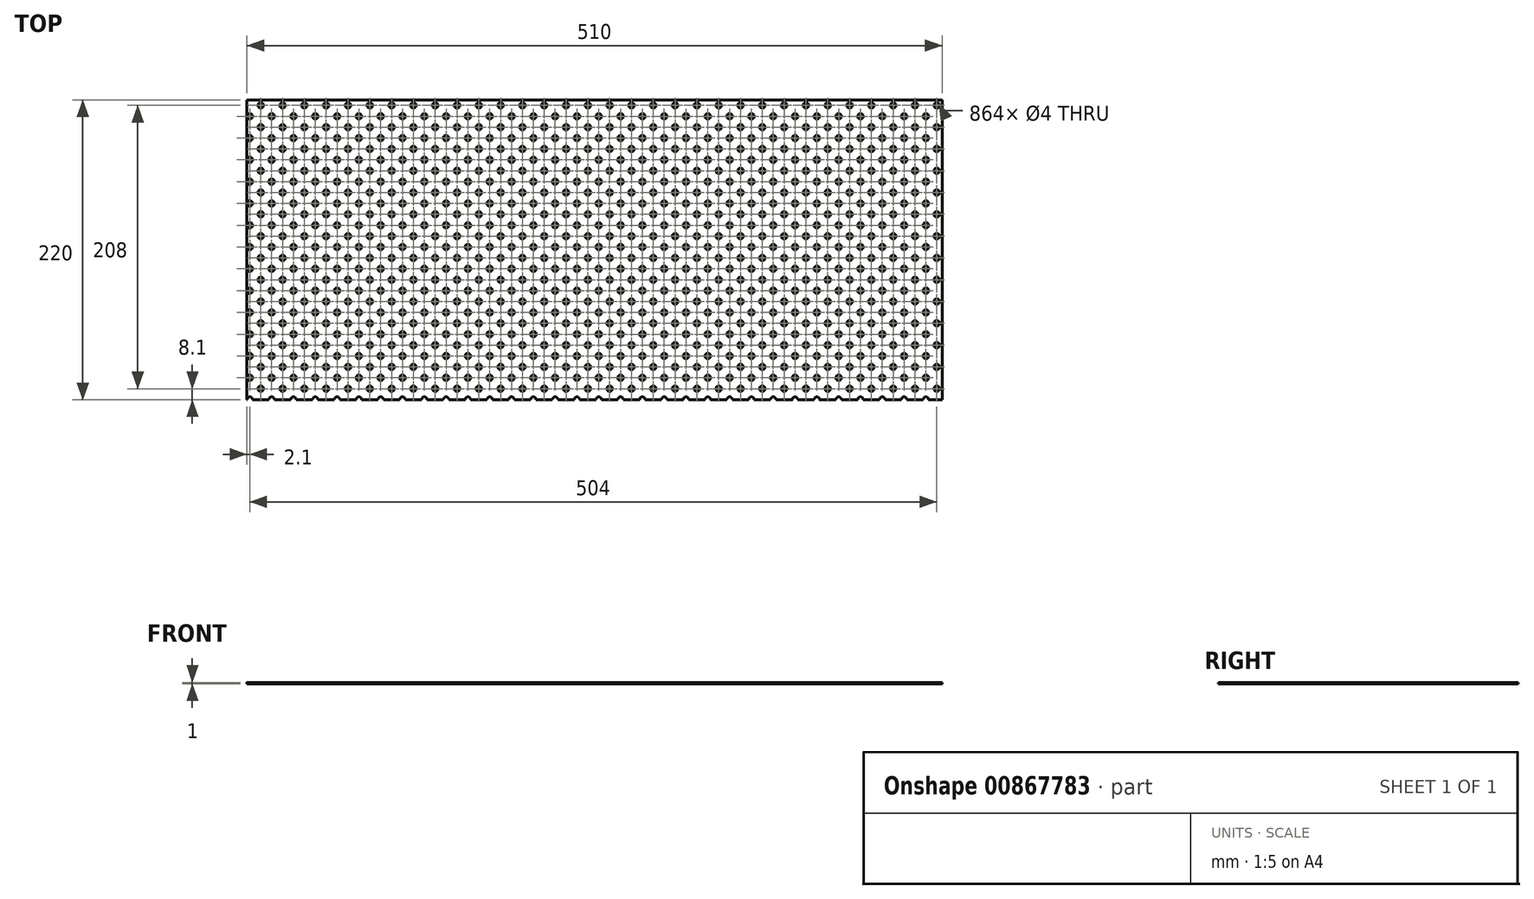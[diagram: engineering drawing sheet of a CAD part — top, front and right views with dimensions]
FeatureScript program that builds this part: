
annotation { "Feature Type Name" : "Feature", "Feature Type Description" : "" }
export const myFeature = defineFeature(function(context is Context, id is Id, definition is map)
    precondition{}
    {
        {
            var Q0;
            Q0=qCreatedBy(makeId("Top.planeOp"),FACE);
            var sketch = newSketch(context, id + "F0", { "sketchPlane" : qUnion([Q0])});
            skLineSegment(sketch, "E0.bottom", {"start": v(255, -110) * mm, "end": v(-255, -110) * mm});
            skLineSegment(sketch, "E0.top", {"start": v(255, 110) * mm, "end": v(-255, 110) * mm});
            skLineSegment(sketch, "E0.left", {"start": v(255, -110) * mm, "end": v(255, 110) * mm});
            skLineSegment(sketch, "E0.right", {"start": v(-255, -110) * mm, "end": v(-255, 110) * mm});
            skPoint(sketch, "E0.middle", {"position": v(0, 0) * mm});
            skCircle(sketch, "E1", {"center": v(-252.9, -109.9) * mm, "radius": 2 * mm});
            skCircle(sketch, "E2.0.1.0", {"center": v(-252.9, -93.9) * mm, "radius": 2 * mm});
            skCircle(sketch, "E2.0.2.0", {"center": v(-252.9, -77.9) * mm, "radius": 2 * mm});
            skCircle(sketch, "E2.0.3.0", {"center": v(-252.9, -61.9) * mm, "radius": 2 * mm});
            skCircle(sketch, "E2.0.4.0", {"center": v(-252.9, -45.9) * mm, "radius": 2 * mm});
            skCircle(sketch, "E2.0.5.0", {"center": v(-252.9, -29.9) * mm, "radius": 2 * mm});
            skCircle(sketch, "E2.0.6.0", {"center": v(-252.9, -13.9) * mm, "radius": 2 * mm});
            skCircle(sketch, "E2.0.7.0", {"center": v(-252.9, 2.1) * mm, "radius": 2 * mm});
            skCircle(sketch, "E2.1.0.0", {"center": v(-236.9, -109.9) * mm, "radius": 2 * mm});
            skCircle(sketch, "E2.1.1.0", {"center": v(-236.9, -93.9) * mm, "radius": 2 * mm});
            skCircle(sketch, "E2.1.2.0", {"center": v(-236.9, -77.9) * mm, "radius": 2 * mm});
            skCircle(sketch, "E2.1.3.0", {"center": v(-236.9, -61.9) * mm, "radius": 2 * mm});
            skCircle(sketch, "E2.1.4.0", {"center": v(-236.9, -45.9) * mm, "radius": 2 * mm});
            skCircle(sketch, "E2.1.5.0", {"center": v(-236.9, -29.9) * mm, "radius": 2 * mm});
            skCircle(sketch, "E2.1.6.0", {"center": v(-236.9, -13.9) * mm, "radius": 2 * mm});
            skCircle(sketch, "E2.1.7.0", {"center": v(-236.9, 2.1) * mm, "radius": 2 * mm});
            skCircle(sketch, "E2.2.0.0", {"center": v(-220.9, -109.9) * mm, "radius": 2 * mm});
            skCircle(sketch, "E2.2.1.0", {"center": v(-220.9, -93.9) * mm, "radius": 2 * mm});
            skCircle(sketch, "E2.2.2.0", {"center": v(-220.9, -77.9) * mm, "radius": 2 * mm});
            skCircle(sketch, "E2.2.3.0", {"center": v(-220.9, -61.9) * mm, "radius": 2 * mm});
            skCircle(sketch, "E2.2.4.0", {"center": v(-220.9, -45.9) * mm, "radius": 2 * mm});
            skCircle(sketch, "E2.2.5.0", {"center": v(-220.9, -29.9) * mm, "radius": 2 * mm});
            skCircle(sketch, "E2.2.6.0", {"center": v(-220.9, -13.9) * mm, "radius": 2 * mm});
            skCircle(sketch, "E2.2.7.0", {"center": v(-220.9, 2.1) * mm, "radius": 2 * mm});
            skCircle(sketch, "E2.3.0.0", {"center": v(-204.9, -109.9) * mm, "radius": 2 * mm});
            skCircle(sketch, "E2.3.1.0", {"center": v(-204.9, -93.9) * mm, "radius": 2 * mm});
            skCircle(sketch, "E2.3.2.0", {"center": v(-204.9, -77.9) * mm, "radius": 2 * mm});
            skCircle(sketch, "E2.3.3.0", {"center": v(-204.9, -61.9) * mm, "radius": 2 * mm});
            skCircle(sketch, "E2.3.4.0", {"center": v(-204.9, -45.9) * mm, "radius": 2 * mm});
            skCircle(sketch, "E2.3.5.0", {"center": v(-204.9, -29.9) * mm, "radius": 2 * mm});
            skCircle(sketch, "E2.3.6.0", {"center": v(-204.9, -13.9) * mm, "radius": 2 * mm});
            skCircle(sketch, "E2.3.7.0", {"center": v(-204.9, 2.1) * mm, "radius": 2 * mm});
            skCircle(sketch, "E2.4.0.0", {"center": v(-188.9, -109.9) * mm, "radius": 2 * mm});
            skCircle(sketch, "E2.4.1.0", {"center": v(-188.9, -93.9) * mm, "radius": 2 * mm});
            skCircle(sketch, "E2.4.2.0", {"center": v(-188.9, -77.9) * mm, "radius": 2 * mm});
            skCircle(sketch, "E2.4.3.0", {"center": v(-188.9, -61.9) * mm, "radius": 2 * mm});
            skCircle(sketch, "E2.4.4.0", {"center": v(-188.9, -45.9) * mm, "radius": 2 * mm});
            skCircle(sketch, "E2.4.5.0", {"center": v(-188.9, -29.9) * mm, "radius": 2 * mm});
            skCircle(sketch, "E2.4.6.0", {"center": v(-188.9, -13.9) * mm, "radius": 2 * mm});
            skCircle(sketch, "E2.4.7.0", {"center": v(-188.9, 2.1) * mm, "radius": 2 * mm});
            skCircle(sketch, "E2.5.0.0", {"center": v(-172.9, -109.9) * mm, "radius": 2 * mm});
            skCircle(sketch, "E2.5.1.0", {"center": v(-172.9, -93.9) * mm, "radius": 2 * mm});
            skCircle(sketch, "E2.5.2.0", {"center": v(-172.9, -77.9) * mm, "radius": 2 * mm});
            skCircle(sketch, "E2.5.3.0", {"center": v(-172.9, -61.9) * mm, "radius": 2 * mm});
            skCircle(sketch, "E2.5.4.0", {"center": v(-172.9, -45.9) * mm, "radius": 2 * mm});
            skCircle(sketch, "E2.5.5.0", {"center": v(-172.9, -29.9) * mm, "radius": 2 * mm});
            skCircle(sketch, "E2.5.6.0", {"center": v(-172.9, -13.9) * mm, "radius": 2 * mm});
            skCircle(sketch, "E2.5.7.0", {"center": v(-172.9, 2.1) * mm, "radius": 2 * mm});
            skCircle(sketch, "E2.6.0.0", {"center": v(-156.9, -109.9) * mm, "radius": 2 * mm});
            skCircle(sketch, "E2.6.1.0", {"center": v(-156.9, -93.9) * mm, "radius": 2 * mm});
            skCircle(sketch, "E2.6.2.0", {"center": v(-156.9, -77.9) * mm, "radius": 2 * mm});
            skCircle(sketch, "E2.6.3.0", {"center": v(-156.9, -61.9) * mm, "radius": 2 * mm});
            skCircle(sketch, "E2.6.4.0", {"center": v(-156.9, -45.9) * mm, "radius": 2 * mm});
            skCircle(sketch, "E2.6.5.0", {"center": v(-156.9, -29.9) * mm, "radius": 2 * mm});
            skCircle(sketch, "E2.6.6.0", {"center": v(-156.9, -13.9) * mm, "radius": 2 * mm});
            skCircle(sketch, "E2.6.7.0", {"center": v(-156.9, 2.1) * mm, "radius": 2 * mm});
            skCircle(sketch, "E2.7.0.0", {"center": v(-140.9, -109.9) * mm, "radius": 2 * mm});
            skCircle(sketch, "E2.7.1.0", {"center": v(-140.9, -93.9) * mm, "radius": 2 * mm});
            skCircle(sketch, "E2.7.2.0", {"center": v(-140.9, -77.9) * mm, "radius": 2 * mm});
            skCircle(sketch, "E2.7.3.0", {"center": v(-140.9, -61.9) * mm, "radius": 2 * mm});
            skCircle(sketch, "E2.7.4.0", {"center": v(-140.9, -45.9) * mm, "radius": 2 * mm});
            skCircle(sketch, "E2.7.5.0", {"center": v(-140.9, -29.9) * mm, "radius": 2 * mm});
            skCircle(sketch, "E2.7.6.0", {"center": v(-140.9, -13.9) * mm, "radius": 2 * mm});
            skCircle(sketch, "E2.7.7.0", {"center": v(-140.9, 2.1) * mm, "radius": 2 * mm});
            skCircle(sketch, "E2.8.0.0", {"center": v(-124.9, -109.9) * mm, "radius": 2 * mm});
            skCircle(sketch, "E2.8.1.0", {"center": v(-124.9, -93.9) * mm, "radius": 2 * mm});
            skCircle(sketch, "E2.8.2.0", {"center": v(-124.9, -77.9) * mm, "radius": 2 * mm});
            skCircle(sketch, "E2.8.3.0", {"center": v(-124.9, -61.9) * mm, "radius": 2 * mm});
            skCircle(sketch, "E2.8.4.0", {"center": v(-124.9, -45.9) * mm, "radius": 2 * mm});
            skCircle(sketch, "E2.8.5.0", {"center": v(-124.9, -29.9) * mm, "radius": 2 * mm});
            skCircle(sketch, "E2.8.6.0", {"center": v(-124.9, -13.9) * mm, "radius": 2 * mm});
            skCircle(sketch, "E2.8.7.0", {"center": v(-124.9, 2.1) * mm, "radius": 2 * mm});
            skCircle(sketch, "E2.9.0.0", {"center": v(-108.9, -109.9) * mm, "radius": 2 * mm});
            skCircle(sketch, "E2.9.1.0", {"center": v(-108.9, -93.9) * mm, "radius": 2 * mm});
            skCircle(sketch, "E2.9.2.0", {"center": v(-108.9, -77.9) * mm, "radius": 2 * mm});
            skCircle(sketch, "E2.9.3.0", {"center": v(-108.9, -61.9) * mm, "radius": 2 * mm});
            skCircle(sketch, "E2.9.4.0", {"center": v(-108.9, -45.9) * mm, "radius": 2 * mm});
            skCircle(sketch, "E2.9.5.0", {"center": v(-108.9, -29.9) * mm, "radius": 2 * mm});
            skCircle(sketch, "E2.9.6.0", {"center": v(-108.9, -13.9) * mm, "radius": 2 * mm});
            skCircle(sketch, "E2.9.7.0", {"center": v(-108.9, 2.1) * mm, "radius": 2 * mm});
            skCircle(sketch, "E2.10.0.0", {"center": v(-92.9, -109.9) * mm, "radius": 2 * mm});
            skCircle(sketch, "E2.10.1.0", {"center": v(-92.9, -93.9) * mm, "radius": 2 * mm});
            skCircle(sketch, "E2.10.2.0", {"center": v(-92.9, -77.9) * mm, "radius": 2 * mm});
            skCircle(sketch, "E2.10.3.0", {"center": v(-92.9, -61.9) * mm, "radius": 2 * mm});
            skCircle(sketch, "E2.10.4.0", {"center": v(-92.9, -45.9) * mm, "radius": 2 * mm});
            skCircle(sketch, "E2.10.5.0", {"center": v(-92.9, -29.9) * mm, "radius": 2 * mm});
            skCircle(sketch, "E2.10.6.0", {"center": v(-92.9, -13.9) * mm, "radius": 2 * mm});
            skCircle(sketch, "E2.10.7.0", {"center": v(-92.9, 2.1) * mm, "radius": 2 * mm});
            skCircle(sketch, "E2.11.0.0", {"center": v(-76.9, -109.9) * mm, "radius": 2 * mm});
            skCircle(sketch, "E2.11.1.0", {"center": v(-76.9, -93.9) * mm, "radius": 2 * mm});
            skCircle(sketch, "E2.11.2.0", {"center": v(-76.9, -77.9) * mm, "radius": 2 * mm});
            skCircle(sketch, "E2.11.3.0", {"center": v(-76.9, -61.9) * mm, "radius": 2 * mm});
            skCircle(sketch, "E2.11.4.0", {"center": v(-76.9, -45.9) * mm, "radius": 2 * mm});
            skCircle(sketch, "E2.11.5.0", {"center": v(-76.9, -29.9) * mm, "radius": 2 * mm});
            skCircle(sketch, "E2.11.6.0", {"center": v(-76.9, -13.9) * mm, "radius": 2 * mm});
            skCircle(sketch, "E2.11.7.0", {"center": v(-76.9, 2.1) * mm, "radius": 2 * mm});
            skCircle(sketch, "E2.12.0.0", {"center": v(-60.9, -109.9) * mm, "radius": 2 * mm});
            skCircle(sketch, "E2.12.1.0", {"center": v(-60.9, -93.9) * mm, "radius": 2 * mm});
            skCircle(sketch, "E2.12.2.0", {"center": v(-60.9, -77.9) * mm, "radius": 2 * mm});
            skCircle(sketch, "E2.12.3.0", {"center": v(-60.9, -61.9) * mm, "radius": 2 * mm});
            skCircle(sketch, "E2.12.4.0", {"center": v(-60.9, -45.9) * mm, "radius": 2 * mm});
            skCircle(sketch, "E2.12.5.0", {"center": v(-60.9, -29.9) * mm, "radius": 2 * mm});
            skCircle(sketch, "E2.12.6.0", {"center": v(-60.9, -13.9) * mm, "radius": 2 * mm});
            skCircle(sketch, "E2.12.7.0", {"center": v(-60.9, 2.1) * mm, "radius": 2 * mm});
            skCircle(sketch, "E2.13.0.0", {"center": v(-44.9, -109.9) * mm, "radius": 2 * mm});
            skCircle(sketch, "E2.13.1.0", {"center": v(-44.9, -93.9) * mm, "radius": 2 * mm});
            skCircle(sketch, "E2.13.2.0", {"center": v(-44.9, -77.9) * mm, "radius": 2 * mm});
            skCircle(sketch, "E2.13.3.0", {"center": v(-44.9, -61.9) * mm, "radius": 2 * mm});
            skCircle(sketch, "E2.13.4.0", {"center": v(-44.9, -45.9) * mm, "radius": 2 * mm});
            skCircle(sketch, "E2.13.5.0", {"center": v(-44.9, -29.9) * mm, "radius": 2 * mm});
            skCircle(sketch, "E2.13.6.0", {"center": v(-44.9, -13.9) * mm, "radius": 2 * mm});
            skCircle(sketch, "E2.13.7.0", {"center": v(-44.9, 2.1) * mm, "radius": 2 * mm});
            skCircle(sketch, "E2.14.0.0", {"center": v(-28.9, -109.9) * mm, "radius": 2 * mm});
            skCircle(sketch, "E2.14.1.0", {"center": v(-28.9, -93.9) * mm, "radius": 2 * mm});
            skCircle(sketch, "E2.14.2.0", {"center": v(-28.9, -77.9) * mm, "radius": 2 * mm});
            skCircle(sketch, "E2.14.3.0", {"center": v(-28.9, -61.9) * mm, "radius": 2 * mm});
            skCircle(sketch, "E2.14.4.0", {"center": v(-28.9, -45.9) * mm, "radius": 2 * mm});
            skCircle(sketch, "E2.14.5.0", {"center": v(-28.9, -29.9) * mm, "radius": 2 * mm});
            skCircle(sketch, "E2.14.6.0", {"center": v(-28.9, -13.9) * mm, "radius": 2 * mm});
            skCircle(sketch, "E2.14.7.0", {"center": v(-28.9, 2.1) * mm, "radius": 2 * mm});
            skCircle(sketch, "E2.15.0.0", {"center": v(-12.9, -109.9) * mm, "radius": 2 * mm});
            skCircle(sketch, "E2.15.1.0", {"center": v(-12.9, -93.9) * mm, "radius": 2 * mm});
            skCircle(sketch, "E2.15.2.0", {"center": v(-12.9, -77.9) * mm, "radius": 2 * mm});
            skCircle(sketch, "E2.15.3.0", {"center": v(-12.9, -61.9) * mm, "radius": 2 * mm});
            skCircle(sketch, "E2.15.4.0", {"center": v(-12.9, -45.9) * mm, "radius": 2 * mm});
            skCircle(sketch, "E2.15.5.0", {"center": v(-12.9, -29.9) * mm, "radius": 2 * mm});
            skCircle(sketch, "E2.15.6.0", {"center": v(-12.9, -13.9) * mm, "radius": 2 * mm});
            skCircle(sketch, "E2.15.7.0", {"center": v(-12.9, 2.1) * mm, "radius": 2 * mm});
            skCircle(sketch, "E2.16.0.0", {"center": v(3.1, -109.9) * mm, "radius": 2 * mm});
            skCircle(sketch, "E2.16.1.0", {"center": v(3.1, -93.9) * mm, "radius": 2 * mm});
            skCircle(sketch, "E2.16.2.0", {"center": v(3.1, -77.9) * mm, "radius": 2 * mm});
            skCircle(sketch, "E2.16.3.0", {"center": v(3.1, -61.9) * mm, "radius": 2 * mm});
            skCircle(sketch, "E2.16.4.0", {"center": v(3.1, -45.9) * mm, "radius": 2 * mm});
            skCircle(sketch, "E2.16.5.0", {"center": v(3.1, -29.9) * mm, "radius": 2 * mm});
            skCircle(sketch, "E2.16.6.0", {"center": v(3.1, -13.9) * mm, "radius": 2 * mm});
            skCircle(sketch, "E2.16.7.0", {"center": v(3.1, 2.1) * mm, "radius": 2 * mm});
            skCircle(sketch, "E2.17.0.0", {"center": v(19.1, -109.9) * mm, "radius": 2 * mm});
            skCircle(sketch, "E2.17.1.0", {"center": v(19.1, -93.9) * mm, "radius": 2 * mm});
            skCircle(sketch, "E2.17.2.0", {"center": v(19.1, -77.9) * mm, "radius": 2 * mm});
            skCircle(sketch, "E2.17.3.0", {"center": v(19.1, -61.9) * mm, "radius": 2 * mm});
            skCircle(sketch, "E2.17.4.0", {"center": v(19.1, -45.9) * mm, "radius": 2 * mm});
            skCircle(sketch, "E2.17.5.0", {"center": v(19.1, -29.9) * mm, "radius": 2 * mm});
            skCircle(sketch, "E2.17.6.0", {"center": v(19.1, -13.9) * mm, "radius": 2 * mm});
            skCircle(sketch, "E2.17.7.0", {"center": v(19.1, 2.1) * mm, "radius": 2 * mm});
            skCircle(sketch, "E2.18.0.0", {"center": v(35.1, -109.9) * mm, "radius": 2 * mm});
            skCircle(sketch, "E2.18.1.0", {"center": v(35.1, -93.9) * mm, "radius": 2 * mm});
            skCircle(sketch, "E2.18.2.0", {"center": v(35.1, -77.9) * mm, "radius": 2 * mm});
            skCircle(sketch, "E2.18.3.0", {"center": v(35.1, -61.9) * mm, "radius": 2 * mm});
            skCircle(sketch, "E2.18.4.0", {"center": v(35.1, -45.9) * mm, "radius": 2 * mm});
            skCircle(sketch, "E2.18.5.0", {"center": v(35.1, -29.9) * mm, "radius": 2 * mm});
            skCircle(sketch, "E2.18.6.0", {"center": v(35.1, -13.9) * mm, "radius": 2 * mm});
            skCircle(sketch, "E2.18.7.0", {"center": v(35.1, 2.1) * mm, "radius": 2 * mm});
            skCircle(sketch, "E2.19.0.0", {"center": v(51.1, -109.9) * mm, "radius": 2 * mm});
            skCircle(sketch, "E2.19.1.0", {"center": v(51.1, -93.9) * mm, "radius": 2 * mm});
            skCircle(sketch, "E2.19.2.0", {"center": v(51.1, -77.9) * mm, "radius": 2 * mm});
            skCircle(sketch, "E2.19.3.0", {"center": v(51.1, -61.9) * mm, "radius": 2 * mm});
            skCircle(sketch, "E2.19.4.0", {"center": v(51.1, -45.9) * mm, "radius": 2 * mm});
            skCircle(sketch, "E2.19.5.0", {"center": v(51.1, -29.9) * mm, "radius": 2 * mm});
            skCircle(sketch, "E2.19.6.0", {"center": v(51.1, -13.9) * mm, "radius": 2 * mm});
            skCircle(sketch, "E2.19.7.0", {"center": v(51.1, 2.1) * mm, "radius": 2 * mm});
            skCircle(sketch, "E2.20.0.0", {"center": v(67.1, -109.9) * mm, "radius": 2 * mm});
            skCircle(sketch, "E2.20.1.0", {"center": v(67.1, -93.9) * mm, "radius": 2 * mm});
            skCircle(sketch, "E2.20.2.0", {"center": v(67.1, -77.9) * mm, "radius": 2 * mm});
            skCircle(sketch, "E2.20.3.0", {"center": v(67.1, -61.9) * mm, "radius": 2 * mm});
            skCircle(sketch, "E2.20.4.0", {"center": v(67.1, -45.9) * mm, "radius": 2 * mm});
            skCircle(sketch, "E2.20.5.0", {"center": v(67.1, -29.9) * mm, "radius": 2 * mm});
            skCircle(sketch, "E2.20.6.0", {"center": v(67.1, -13.9) * mm, "radius": 2 * mm});
            skCircle(sketch, "E2.20.7.0", {"center": v(67.1, 2.1) * mm, "radius": 2 * mm});
            skCircle(sketch, "E2.21.0.0", {"center": v(83.1, -109.9) * mm, "radius": 2 * mm});
            skCircle(sketch, "E2.21.1.0", {"center": v(83.1, -93.9) * mm, "radius": 2 * mm});
            skCircle(sketch, "E2.21.2.0", {"center": v(83.1, -77.9) * mm, "radius": 2 * mm});
            skCircle(sketch, "E2.21.3.0", {"center": v(83.1, -61.9) * mm, "radius": 2 * mm});
            skCircle(sketch, "E2.21.4.0", {"center": v(83.1, -45.9) * mm, "radius": 2 * mm});
            skCircle(sketch, "E2.21.5.0", {"center": v(83.1, -29.9) * mm, "radius": 2 * mm});
            skCircle(sketch, "E2.21.6.0", {"center": v(83.1, -13.9) * mm, "radius": 2 * mm});
            skCircle(sketch, "E2.21.7.0", {"center": v(83.1, 2.1) * mm, "radius": 2 * mm});
            skCircle(sketch, "E2.22.0.0", {"center": v(99.1, -109.9) * mm, "radius": 2 * mm});
            skCircle(sketch, "E2.22.1.0", {"center": v(99.1, -93.9) * mm, "radius": 2 * mm});
            skCircle(sketch, "E2.22.2.0", {"center": v(99.1, -77.9) * mm, "radius": 2 * mm});
            skCircle(sketch, "E2.22.3.0", {"center": v(99.1, -61.9) * mm, "radius": 2 * mm});
            skCircle(sketch, "E2.22.4.0", {"center": v(99.1, -45.9) * mm, "radius": 2 * mm});
            skCircle(sketch, "E2.22.5.0", {"center": v(99.1, -29.9) * mm, "radius": 2 * mm});
            skCircle(sketch, "E2.22.6.0", {"center": v(99.1, -13.9) * mm, "radius": 2 * mm});
            skCircle(sketch, "E2.22.7.0", {"center": v(99.1, 2.1) * mm, "radius": 2 * mm});
            skCircle(sketch, "E2.23.0.0", {"center": v(115.1, -109.9) * mm, "radius": 2 * mm});
            skCircle(sketch, "E2.23.1.0", {"center": v(115.1, -93.9) * mm, "radius": 2 * mm});
            skCircle(sketch, "E2.23.2.0", {"center": v(115.1, -77.9) * mm, "radius": 2 * mm});
            skCircle(sketch, "E2.23.3.0", {"center": v(115.1, -61.9) * mm, "radius": 2 * mm});
            skCircle(sketch, "E2.23.4.0", {"center": v(115.1, -45.9) * mm, "radius": 2 * mm});
            skCircle(sketch, "E2.23.5.0", {"center": v(115.1, -29.9) * mm, "radius": 2 * mm});
            skCircle(sketch, "E2.23.6.0", {"center": v(115.1, -13.9) * mm, "radius": 2 * mm});
            skCircle(sketch, "E2.23.7.0", {"center": v(115.1, 2.1) * mm, "radius": 2 * mm});
            skCircle(sketch, "E2.24.0.0", {"center": v(131.1, -109.9) * mm, "radius": 2 * mm});
            skCircle(sketch, "E2.24.1.0", {"center": v(131.1, -93.9) * mm, "radius": 2 * mm});
            skCircle(sketch, "E2.24.2.0", {"center": v(131.1, -77.9) * mm, "radius": 2 * mm});
            skCircle(sketch, "E2.24.3.0", {"center": v(131.1, -61.9) * mm, "radius": 2 * mm});
            skCircle(sketch, "E2.24.4.0", {"center": v(131.1, -45.9) * mm, "radius": 2 * mm});
            skCircle(sketch, "E2.24.5.0", {"center": v(131.1, -29.9) * mm, "radius": 2 * mm});
            skCircle(sketch, "E2.24.6.0", {"center": v(131.1, -13.9) * mm, "radius": 2 * mm});
            skCircle(sketch, "E2.24.7.0", {"center": v(131.1, 2.1) * mm, "radius": 2 * mm});
            skCircle(sketch, "E2.25.0.0", {"center": v(147.1, -109.9) * mm, "radius": 2 * mm});
            skCircle(sketch, "E2.25.1.0", {"center": v(147.1, -93.9) * mm, "radius": 2 * mm});
            skCircle(sketch, "E2.25.2.0", {"center": v(147.1, -77.9) * mm, "radius": 2 * mm});
            skCircle(sketch, "E2.25.3.0", {"center": v(147.1, -61.9) * mm, "radius": 2 * mm});
            skCircle(sketch, "E2.25.4.0", {"center": v(147.1, -45.9) * mm, "radius": 2 * mm});
            skCircle(sketch, "E2.25.5.0", {"center": v(147.1, -29.9) * mm, "radius": 2 * mm});
            skCircle(sketch, "E2.25.6.0", {"center": v(147.1, -13.9) * mm, "radius": 2 * mm});
            skCircle(sketch, "E2.25.7.0", {"center": v(147.1, 2.1) * mm, "radius": 2 * mm});
            skCircle(sketch, "E2.26.0.0", {"center": v(163.1, -109.9) * mm, "radius": 2 * mm});
            skCircle(sketch, "E2.26.1.0", {"center": v(163.1, -93.9) * mm, "radius": 2 * mm});
            skCircle(sketch, "E2.26.2.0", {"center": v(163.1, -77.9) * mm, "radius": 2 * mm});
            skCircle(sketch, "E2.26.3.0", {"center": v(163.1, -61.9) * mm, "radius": 2 * mm});
            skCircle(sketch, "E2.26.4.0", {"center": v(163.1, -45.9) * mm, "radius": 2 * mm});
            skCircle(sketch, "E2.26.5.0", {"center": v(163.1, -29.9) * mm, "radius": 2 * mm});
            skCircle(sketch, "E2.26.6.0", {"center": v(163.1, -13.9) * mm, "radius": 2 * mm});
            skCircle(sketch, "E2.26.7.0", {"center": v(163.1, 2.1) * mm, "radius": 2 * mm});
            skCircle(sketch, "E2.27.0.0", {"center": v(179.1, -109.9) * mm, "radius": 2 * mm});
            skCircle(sketch, "E2.27.1.0", {"center": v(179.1, -93.9) * mm, "radius": 2 * mm});
            skCircle(sketch, "E2.27.2.0", {"center": v(179.1, -77.9) * mm, "radius": 2 * mm});
            skCircle(sketch, "E2.27.3.0", {"center": v(179.1, -61.9) * mm, "radius": 2 * mm});
            skCircle(sketch, "E2.27.4.0", {"center": v(179.1, -45.9) * mm, "radius": 2 * mm});
            skCircle(sketch, "E2.27.5.0", {"center": v(179.1, -29.9) * mm, "radius": 2 * mm});
            skCircle(sketch, "E2.27.6.0", {"center": v(179.1, -13.9) * mm, "radius": 2 * mm});
            skCircle(sketch, "E2.27.7.0", {"center": v(179.1, 2.1) * mm, "radius": 2 * mm});
            skCircle(sketch, "E2.28.0.0", {"center": v(195.1, -109.9) * mm, "radius": 2 * mm});
            skCircle(sketch, "E2.28.1.0", {"center": v(195.1, -93.9) * mm, "radius": 2 * mm});
            skCircle(sketch, "E2.28.2.0", {"center": v(195.1, -77.9) * mm, "radius": 2 * mm});
            skCircle(sketch, "E2.28.3.0", {"center": v(195.1, -61.9) * mm, "radius": 2 * mm});
            skCircle(sketch, "E2.28.4.0", {"center": v(195.1, -45.9) * mm, "radius": 2 * mm});
            skCircle(sketch, "E2.28.5.0", {"center": v(195.1, -29.9) * mm, "radius": 2 * mm});
            skCircle(sketch, "E2.28.6.0", {"center": v(195.1, -13.9) * mm, "radius": 2 * mm});
            skCircle(sketch, "E2.28.7.0", {"center": v(195.1, 2.1) * mm, "radius": 2 * mm});
            skCircle(sketch, "E2.29.0.0", {"center": v(211.1, -109.9) * mm, "radius": 2 * mm});
            skCircle(sketch, "E2.29.1.0", {"center": v(211.1, -93.9) * mm, "radius": 2 * mm});
            skCircle(sketch, "E2.29.2.0", {"center": v(211.1, -77.9) * mm, "radius": 2 * mm});
            skCircle(sketch, "E2.29.3.0", {"center": v(211.1, -61.9) * mm, "radius": 2 * mm});
            skCircle(sketch, "E2.29.4.0", {"center": v(211.1, -45.9) * mm, "radius": 2 * mm});
            skCircle(sketch, "E2.29.5.0", {"center": v(211.1, -29.9) * mm, "radius": 2 * mm});
            skCircle(sketch, "E2.29.6.0", {"center": v(211.1, -13.9) * mm, "radius": 2 * mm});
            skCircle(sketch, "E2.29.7.0", {"center": v(211.1, 2.1) * mm, "radius": 2 * mm});
            skCircle(sketch, "E2.30.0.0", {"center": v(227.1, -109.9) * mm, "radius": 2 * mm});
            skCircle(sketch, "E2.30.1.0", {"center": v(227.1, -93.9) * mm, "radius": 2 * mm});
            skCircle(sketch, "E2.30.2.0", {"center": v(227.1, -77.9) * mm, "radius": 2 * mm});
            skCircle(sketch, "E2.30.3.0", {"center": v(227.1, -61.9) * mm, "radius": 2 * mm});
            skCircle(sketch, "E2.30.4.0", {"center": v(227.1, -45.9) * mm, "radius": 2 * mm});
            skCircle(sketch, "E2.30.5.0", {"center": v(227.1, -29.9) * mm, "radius": 2 * mm});
            skCircle(sketch, "E2.30.6.0", {"center": v(227.1, -13.9) * mm, "radius": 2 * mm});
            skCircle(sketch, "E2.30.7.0", {"center": v(227.1, 2.1) * mm, "radius": 2 * mm});
            skLineSegment(sketch, "E2.direction1", {"start": v(-252.9, -109.9) * mm, "end": v(-236.9, -109.9) * mm, "construction": true});
            skLineSegment(sketch, "E2.direction2", {"start": v(-252.9, -109.9) * mm, "end": v(-252.9, -93.9) * mm, "construction": true});
            skCircle(sketch, "E3", {"center": v(-244.9, -101.9) * mm, "radius": 2 * mm});
            skCircle(sketch, "E4.0.1.0", {"center": v(-244.9, -85.9) * mm, "radius": 2 * mm});
            skCircle(sketch, "E4.0.2.0", {"center": v(-244.9, -69.9) * mm, "radius": 2 * mm});
            skCircle(sketch, "E4.0.3.0", {"center": v(-244.9, -53.9) * mm, "radius": 2 * mm});
            skCircle(sketch, "E4.0.4.0", {"center": v(-244.9, -37.9) * mm, "radius": 2 * mm});
            skCircle(sketch, "E4.0.5.0", {"center": v(-244.9, -21.9) * mm, "radius": 2 * mm});
            skCircle(sketch, "E4.1.0.0", {"center": v(-228.9, -101.9) * mm, "radius": 2 * mm});
            skCircle(sketch, "E4.1.1.0", {"center": v(-228.9, -85.9) * mm, "radius": 2 * mm});
            skCircle(sketch, "E4.1.2.0", {"center": v(-228.9, -69.9) * mm, "radius": 2 * mm});
            skCircle(sketch, "E4.1.3.0", {"center": v(-228.9, -53.9) * mm, "radius": 2 * mm});
            skCircle(sketch, "E4.1.4.0", {"center": v(-228.9, -37.9) * mm, "radius": 2 * mm});
            skCircle(sketch, "E4.1.5.0", {"center": v(-228.9, -21.9) * mm, "radius": 2 * mm});
            skCircle(sketch, "E4.2.0.0", {"center": v(-212.9, -101.9) * mm, "radius": 2 * mm});
            skCircle(sketch, "E4.2.1.0", {"center": v(-212.9, -85.9) * mm, "radius": 2 * mm});
            skCircle(sketch, "E4.2.2.0", {"center": v(-212.9, -69.9) * mm, "radius": 2 * mm});
            skCircle(sketch, "E4.2.3.0", {"center": v(-212.9, -53.9) * mm, "radius": 2 * mm});
            skCircle(sketch, "E4.2.4.0", {"center": v(-212.9, -37.9) * mm, "radius": 2 * mm});
            skCircle(sketch, "E4.2.5.0", {"center": v(-212.9, -21.9) * mm, "radius": 2 * mm});
            skCircle(sketch, "E4.3.0.0", {"center": v(-196.9, -101.9) * mm, "radius": 2 * mm});
            skCircle(sketch, "E4.3.1.0", {"center": v(-196.9, -85.9) * mm, "radius": 2 * mm});
            skCircle(sketch, "E4.3.2.0", {"center": v(-196.9, -69.9) * mm, "radius": 2 * mm});
            skCircle(sketch, "E4.3.3.0", {"center": v(-196.9, -53.9) * mm, "radius": 2 * mm});
            skCircle(sketch, "E4.3.4.0", {"center": v(-196.9, -37.9) * mm, "radius": 2 * mm});
            skCircle(sketch, "E4.3.5.0", {"center": v(-196.9, -21.9) * mm, "radius": 2 * mm});
            skCircle(sketch, "E4.4.0.0", {"center": v(-180.9, -101.9) * mm, "radius": 2 * mm});
            skCircle(sketch, "E4.4.1.0", {"center": v(-180.9, -85.9) * mm, "radius": 2 * mm});
            skCircle(sketch, "E4.4.2.0", {"center": v(-180.9, -69.9) * mm, "radius": 2 * mm});
            skCircle(sketch, "E4.4.3.0", {"center": v(-180.9, -53.9) * mm, "radius": 2 * mm});
            skCircle(sketch, "E4.4.4.0", {"center": v(-180.9, -37.9) * mm, "radius": 2 * mm});
            skCircle(sketch, "E4.4.5.0", {"center": v(-180.9, -21.9) * mm, "radius": 2 * mm});
            skCircle(sketch, "E4.5.0.0", {"center": v(-164.9, -101.9) * mm, "radius": 2 * mm});
            skCircle(sketch, "E4.5.1.0", {"center": v(-164.9, -85.9) * mm, "radius": 2 * mm});
            skCircle(sketch, "E4.5.2.0", {"center": v(-164.9, -69.9) * mm, "radius": 2 * mm});
            skCircle(sketch, "E4.5.3.0", {"center": v(-164.9, -53.9) * mm, "radius": 2 * mm});
            skCircle(sketch, "E4.5.4.0", {"center": v(-164.9, -37.9) * mm, "radius": 2 * mm});
            skCircle(sketch, "E4.5.5.0", {"center": v(-164.9, -21.9) * mm, "radius": 2 * mm});
            skCircle(sketch, "E4.6.0.0", {"center": v(-148.9, -101.9) * mm, "radius": 2 * mm});
            skCircle(sketch, "E4.6.1.0", {"center": v(-148.9, -85.9) * mm, "radius": 2 * mm});
            skCircle(sketch, "E4.6.2.0", {"center": v(-148.9, -69.9) * mm, "radius": 2 * mm});
            skCircle(sketch, "E4.6.3.0", {"center": v(-148.9, -53.9) * mm, "radius": 2 * mm});
            skCircle(sketch, "E4.6.4.0", {"center": v(-148.9, -37.9) * mm, "radius": 2 * mm});
            skCircle(sketch, "E4.6.5.0", {"center": v(-148.9, -21.9) * mm, "radius": 2 * mm});
            skCircle(sketch, "E4.7.0.0", {"center": v(-132.9, -101.9) * mm, "radius": 2 * mm});
            skCircle(sketch, "E4.7.1.0", {"center": v(-132.9, -85.9) * mm, "radius": 2 * mm});
            skCircle(sketch, "E4.7.2.0", {"center": v(-132.9, -69.9) * mm, "radius": 2 * mm});
            skCircle(sketch, "E4.7.3.0", {"center": v(-132.9, -53.9) * mm, "radius": 2 * mm});
            skCircle(sketch, "E4.7.4.0", {"center": v(-132.9, -37.9) * mm, "radius": 2 * mm});
            skCircle(sketch, "E4.7.5.0", {"center": v(-132.9, -21.9) * mm, "radius": 2 * mm});
            skCircle(sketch, "E4.8.0.0", {"center": v(-116.9, -101.9) * mm, "radius": 2 * mm});
            skCircle(sketch, "E4.8.1.0", {"center": v(-116.9, -85.9) * mm, "radius": 2 * mm});
            skCircle(sketch, "E4.8.2.0", {"center": v(-116.9, -69.9) * mm, "radius": 2 * mm});
            skCircle(sketch, "E4.8.3.0", {"center": v(-116.9, -53.9) * mm, "radius": 2 * mm});
            skCircle(sketch, "E4.8.4.0", {"center": v(-116.9, -37.9) * mm, "radius": 2 * mm});
            skCircle(sketch, "E4.8.5.0", {"center": v(-116.9, -21.9) * mm, "radius": 2 * mm});
            skCircle(sketch, "E4.9.0.0", {"center": v(-100.9, -101.9) * mm, "radius": 2 * mm});
            skCircle(sketch, "E4.9.1.0", {"center": v(-100.9, -85.9) * mm, "radius": 2 * mm});
            skCircle(sketch, "E4.9.2.0", {"center": v(-100.9, -69.9) * mm, "radius": 2 * mm});
            skCircle(sketch, "E4.9.3.0", {"center": v(-100.9, -53.9) * mm, "radius": 2 * mm});
            skCircle(sketch, "E4.9.4.0", {"center": v(-100.9, -37.9) * mm, "radius": 2 * mm});
            skCircle(sketch, "E4.9.5.0", {"center": v(-100.9, -21.9) * mm, "radius": 2 * mm});
            skCircle(sketch, "E4.10.0.0", {"center": v(-84.9, -101.9) * mm, "radius": 2 * mm});
            skCircle(sketch, "E4.10.1.0", {"center": v(-84.9, -85.9) * mm, "radius": 2 * mm});
            skCircle(sketch, "E4.10.2.0", {"center": v(-84.9, -69.9) * mm, "radius": 2 * mm});
            skCircle(sketch, "E4.10.3.0", {"center": v(-84.9, -53.9) * mm, "radius": 2 * mm});
            skCircle(sketch, "E4.10.4.0", {"center": v(-84.9, -37.9) * mm, "radius": 2 * mm});
            skCircle(sketch, "E4.10.5.0", {"center": v(-84.9, -21.9) * mm, "radius": 2 * mm});
            skCircle(sketch, "E4.11.0.0", {"center": v(-68.9, -101.9) * mm, "radius": 2 * mm});
            skCircle(sketch, "E4.11.1.0", {"center": v(-68.9, -85.9) * mm, "radius": 2 * mm});
            skCircle(sketch, "E4.11.2.0", {"center": v(-68.9, -69.9) * mm, "radius": 2 * mm});
            skCircle(sketch, "E4.11.3.0", {"center": v(-68.9, -53.9) * mm, "radius": 2 * mm});
            skCircle(sketch, "E4.11.4.0", {"center": v(-68.9, -37.9) * mm, "radius": 2 * mm});
            skCircle(sketch, "E4.11.5.0", {"center": v(-68.9, -21.9) * mm, "radius": 2 * mm});
            skCircle(sketch, "E4.12.0.0", {"center": v(-52.9, -101.9) * mm, "radius": 2 * mm});
            skCircle(sketch, "E4.12.1.0", {"center": v(-52.9, -85.9) * mm, "radius": 2 * mm});
            skCircle(sketch, "E4.12.2.0", {"center": v(-52.9, -69.9) * mm, "radius": 2 * mm});
            skCircle(sketch, "E4.12.3.0", {"center": v(-52.9, -53.9) * mm, "radius": 2 * mm});
            skCircle(sketch, "E4.12.4.0", {"center": v(-52.9, -37.9) * mm, "radius": 2 * mm});
            skCircle(sketch, "E4.12.5.0", {"center": v(-52.9, -21.9) * mm, "radius": 2 * mm});
            skCircle(sketch, "E4.13.0.0", {"center": v(-36.9, -101.9) * mm, "radius": 2 * mm});
            skCircle(sketch, "E4.13.1.0", {"center": v(-36.9, -85.9) * mm, "radius": 2 * mm});
            skCircle(sketch, "E4.13.2.0", {"center": v(-36.9, -69.9) * mm, "radius": 2 * mm});
            skCircle(sketch, "E4.13.3.0", {"center": v(-36.9, -53.9) * mm, "radius": 2 * mm});
            skCircle(sketch, "E4.13.4.0", {"center": v(-36.9, -37.9) * mm, "radius": 2 * mm});
            skCircle(sketch, "E4.13.5.0", {"center": v(-36.9, -21.9) * mm, "radius": 2 * mm});
            skCircle(sketch, "E4.14.0.0", {"center": v(-20.9, -101.9) * mm, "radius": 2 * mm});
            skCircle(sketch, "E4.14.1.0", {"center": v(-20.9, -85.9) * mm, "radius": 2 * mm});
            skCircle(sketch, "E4.14.2.0", {"center": v(-20.9, -69.9) * mm, "radius": 2 * mm});
            skCircle(sketch, "E4.14.3.0", {"center": v(-20.9, -53.9) * mm, "radius": 2 * mm});
            skCircle(sketch, "E4.14.4.0", {"center": v(-20.9, -37.9) * mm, "radius": 2 * mm});
            skCircle(sketch, "E4.14.5.0", {"center": v(-20.9, -21.9) * mm, "radius": 2 * mm});
            skCircle(sketch, "E4.15.0.0", {"center": v(-4.9, -101.9) * mm, "radius": 2 * mm});
            skCircle(sketch, "E4.15.1.0", {"center": v(-4.9, -85.9) * mm, "radius": 2 * mm});
            skCircle(sketch, "E4.15.2.0", {"center": v(-4.9, -69.9) * mm, "radius": 2 * mm});
            skCircle(sketch, "E4.15.3.0", {"center": v(-4.9, -53.9) * mm, "radius": 2 * mm});
            skCircle(sketch, "E4.15.4.0", {"center": v(-4.9, -37.9) * mm, "radius": 2 * mm});
            skCircle(sketch, "E4.15.5.0", {"center": v(-4.9, -21.9) * mm, "radius": 2 * mm});
            skCircle(sketch, "E4.16.0.0", {"center": v(11.1, -101.9) * mm, "radius": 2 * mm});
            skCircle(sketch, "E4.16.1.0", {"center": v(11.1, -85.9) * mm, "radius": 2 * mm});
            skCircle(sketch, "E4.16.2.0", {"center": v(11.1, -69.9) * mm, "radius": 2 * mm});
            skCircle(sketch, "E4.16.3.0", {"center": v(11.1, -53.9) * mm, "radius": 2 * mm});
            skCircle(sketch, "E4.16.4.0", {"center": v(11.1, -37.9) * mm, "radius": 2 * mm});
            skCircle(sketch, "E4.16.5.0", {"center": v(11.1, -21.9) * mm, "radius": 2 * mm});
            skCircle(sketch, "E4.17.0.0", {"center": v(27.1, -101.9) * mm, "radius": 2 * mm});
            skCircle(sketch, "E4.17.1.0", {"center": v(27.1, -85.9) * mm, "radius": 2 * mm});
            skCircle(sketch, "E4.17.2.0", {"center": v(27.1, -69.9) * mm, "radius": 2 * mm});
            skCircle(sketch, "E4.17.3.0", {"center": v(27.1, -53.9) * mm, "radius": 2 * mm});
            skCircle(sketch, "E4.17.4.0", {"center": v(27.1, -37.9) * mm, "radius": 2 * mm});
            skCircle(sketch, "E4.17.5.0", {"center": v(27.1, -21.9) * mm, "radius": 2 * mm});
            skCircle(sketch, "E4.18.0.0", {"center": v(43.1, -101.9) * mm, "radius": 2 * mm});
            skCircle(sketch, "E4.18.1.0", {"center": v(43.1, -85.9) * mm, "radius": 2 * mm});
            skCircle(sketch, "E4.18.2.0", {"center": v(43.1, -69.9) * mm, "radius": 2 * mm});
            skCircle(sketch, "E4.18.3.0", {"center": v(43.1, -53.9) * mm, "radius": 2 * mm});
            skCircle(sketch, "E4.18.4.0", {"center": v(43.1, -37.9) * mm, "radius": 2 * mm});
            skCircle(sketch, "E4.18.5.0", {"center": v(43.1, -21.9) * mm, "radius": 2 * mm});
            skCircle(sketch, "E4.19.0.0", {"center": v(59.1, -101.9) * mm, "radius": 2 * mm});
            skCircle(sketch, "E4.19.1.0", {"center": v(59.1, -85.9) * mm, "radius": 2 * mm});
            skCircle(sketch, "E4.19.2.0", {"center": v(59.1, -69.9) * mm, "radius": 2 * mm});
            skCircle(sketch, "E4.19.3.0", {"center": v(59.1, -53.9) * mm, "radius": 2 * mm});
            skCircle(sketch, "E4.19.4.0", {"center": v(59.1, -37.9) * mm, "radius": 2 * mm});
            skCircle(sketch, "E4.19.5.0", {"center": v(59.1, -21.9) * mm, "radius": 2 * mm});
            skCircle(sketch, "E4.20.0.0", {"center": v(75.1, -101.9) * mm, "radius": 2 * mm});
            skCircle(sketch, "E4.20.1.0", {"center": v(75.1, -85.9) * mm, "radius": 2 * mm});
            skCircle(sketch, "E4.20.2.0", {"center": v(75.1, -69.9) * mm, "radius": 2 * mm});
            skCircle(sketch, "E4.20.3.0", {"center": v(75.1, -53.9) * mm, "radius": 2 * mm});
            skCircle(sketch, "E4.20.4.0", {"center": v(75.1, -37.9) * mm, "radius": 2 * mm});
            skCircle(sketch, "E4.20.5.0", {"center": v(75.1, -21.9) * mm, "radius": 2 * mm});
            skCircle(sketch, "E4.21.0.0", {"center": v(91.1, -101.9) * mm, "radius": 2 * mm});
            skCircle(sketch, "E4.21.1.0", {"center": v(91.1, -85.9) * mm, "radius": 2 * mm});
            skCircle(sketch, "E4.21.2.0", {"center": v(91.1, -69.9) * mm, "radius": 2 * mm});
            skCircle(sketch, "E4.21.3.0", {"center": v(91.1, -53.9) * mm, "radius": 2 * mm});
            skCircle(sketch, "E4.21.4.0", {"center": v(91.1, -37.9) * mm, "radius": 2 * mm});
            skCircle(sketch, "E4.21.5.0", {"center": v(91.1, -21.9) * mm, "radius": 2 * mm});
            skCircle(sketch, "E4.22.0.0", {"center": v(107.1, -101.9) * mm, "radius": 2 * mm});
            skCircle(sketch, "E4.22.1.0", {"center": v(107.1, -85.9) * mm, "radius": 2 * mm});
            skCircle(sketch, "E4.22.2.0", {"center": v(107.1, -69.9) * mm, "radius": 2 * mm});
            skCircle(sketch, "E4.22.3.0", {"center": v(107.1, -53.9) * mm, "radius": 2 * mm});
            skCircle(sketch, "E4.22.4.0", {"center": v(107.1, -37.9) * mm, "radius": 2 * mm});
            skCircle(sketch, "E4.22.5.0", {"center": v(107.1, -21.9) * mm, "radius": 2 * mm});
            skCircle(sketch, "E4.23.0.0", {"center": v(123.1, -101.9) * mm, "radius": 2 * mm});
            skCircle(sketch, "E4.23.1.0", {"center": v(123.1, -85.9) * mm, "radius": 2 * mm});
            skCircle(sketch, "E4.23.2.0", {"center": v(123.1, -69.9) * mm, "radius": 2 * mm});
            skCircle(sketch, "E4.23.3.0", {"center": v(123.1, -53.9) * mm, "radius": 2 * mm});
            skCircle(sketch, "E4.23.4.0", {"center": v(123.1, -37.9) * mm, "radius": 2 * mm});
            skCircle(sketch, "E4.23.5.0", {"center": v(123.1, -21.9) * mm, "radius": 2 * mm});
            skCircle(sketch, "E4.24.0.0", {"center": v(139.1, -101.9) * mm, "radius": 2 * mm});
            skCircle(sketch, "E4.24.1.0", {"center": v(139.1, -85.9) * mm, "radius": 2 * mm});
            skCircle(sketch, "E4.24.2.0", {"center": v(139.1, -69.9) * mm, "radius": 2 * mm});
            skCircle(sketch, "E4.24.3.0", {"center": v(139.1, -53.9) * mm, "radius": 2 * mm});
            skCircle(sketch, "E4.24.4.0", {"center": v(139.1, -37.9) * mm, "radius": 2 * mm});
            skCircle(sketch, "E4.24.5.0", {"center": v(139.1, -21.9) * mm, "radius": 2 * mm});
            skCircle(sketch, "E4.25.0.0", {"center": v(155.1, -101.9) * mm, "radius": 2 * mm});
            skCircle(sketch, "E4.25.1.0", {"center": v(155.1, -85.9) * mm, "radius": 2 * mm});
            skCircle(sketch, "E4.25.2.0", {"center": v(155.1, -69.9) * mm, "radius": 2 * mm});
            skCircle(sketch, "E4.25.3.0", {"center": v(155.1, -53.9) * mm, "radius": 2 * mm});
            skCircle(sketch, "E4.25.4.0", {"center": v(155.1, -37.9) * mm, "radius": 2 * mm});
            skCircle(sketch, "E4.25.5.0", {"center": v(155.1, -21.9) * mm, "radius": 2 * mm});
            skCircle(sketch, "E4.26.0.0", {"center": v(171.1, -101.9) * mm, "radius": 2 * mm});
            skCircle(sketch, "E4.26.1.0", {"center": v(171.1, -85.9) * mm, "radius": 2 * mm});
            skCircle(sketch, "E4.26.2.0", {"center": v(171.1, -69.9) * mm, "radius": 2 * mm});
            skCircle(sketch, "E4.26.3.0", {"center": v(171.1, -53.9) * mm, "radius": 2 * mm});
            skCircle(sketch, "E4.26.4.0", {"center": v(171.1, -37.9) * mm, "radius": 2 * mm});
            skCircle(sketch, "E4.26.5.0", {"center": v(171.1, -21.9) * mm, "radius": 2 * mm});
            skCircle(sketch, "E4.27.0.0", {"center": v(187.1, -101.9) * mm, "radius": 2 * mm});
            skCircle(sketch, "E4.27.1.0", {"center": v(187.1, -85.9) * mm, "radius": 2 * mm});
            skCircle(sketch, "E4.27.2.0", {"center": v(187.1, -69.9) * mm, "radius": 2 * mm});
            skCircle(sketch, "E4.27.3.0", {"center": v(187.1, -53.9) * mm, "radius": 2 * mm});
            skCircle(sketch, "E4.27.4.0", {"center": v(187.1, -37.9) * mm, "radius": 2 * mm});
            skCircle(sketch, "E4.27.5.0", {"center": v(187.1, -21.9) * mm, "radius": 2 * mm});
            skCircle(sketch, "E4.28.0.0", {"center": v(203.1, -101.9) * mm, "radius": 2 * mm});
            skCircle(sketch, "E4.28.1.0", {"center": v(203.1, -85.9) * mm, "radius": 2 * mm});
            skCircle(sketch, "E4.28.2.0", {"center": v(203.1, -69.9) * mm, "radius": 2 * mm});
            skCircle(sketch, "E4.28.3.0", {"center": v(203.1, -53.9) * mm, "radius": 2 * mm});
            skCircle(sketch, "E4.28.4.0", {"center": v(203.1, -37.9) * mm, "radius": 2 * mm});
            skCircle(sketch, "E4.28.5.0", {"center": v(203.1, -21.9) * mm, "radius": 2 * mm});
            skCircle(sketch, "E4.29.0.0", {"center": v(219.1, -101.9) * mm, "radius": 2 * mm});
            skCircle(sketch, "E4.29.1.0", {"center": v(219.1, -85.9) * mm, "radius": 2 * mm});
            skCircle(sketch, "E4.29.2.0", {"center": v(219.1, -69.9) * mm, "radius": 2 * mm});
            skCircle(sketch, "E4.29.3.0", {"center": v(219.1, -53.9) * mm, "radius": 2 * mm});
            skCircle(sketch, "E4.29.4.0", {"center": v(219.1, -37.9) * mm, "radius": 2 * mm});
            skCircle(sketch, "E4.29.5.0", {"center": v(219.1, -21.9) * mm, "radius": 2 * mm});
            skCircle(sketch, "E4.30.0.0", {"center": v(235.1, -101.9) * mm, "radius": 2 * mm});
            skCircle(sketch, "E4.30.1.0", {"center": v(235.1, -85.9) * mm, "radius": 2 * mm});
            skCircle(sketch, "E4.30.2.0", {"center": v(235.1, -69.9) * mm, "radius": 2 * mm});
            skCircle(sketch, "E4.30.3.0", {"center": v(235.1, -53.9) * mm, "radius": 2 * mm});
            skCircle(sketch, "E4.30.4.0", {"center": v(235.1, -37.9) * mm, "radius": 2 * mm});
            skCircle(sketch, "E4.30.5.0", {"center": v(235.1, -21.9) * mm, "radius": 2 * mm});
            skLineSegment(sketch, "E4.direction1", {"start": v(-244.9, -101.9) * mm, "end": v(-228.9, -101.9) * mm, "construction": true});
            skLineSegment(sketch, "E4.direction2", {"start": v(-244.9, -101.9) * mm, "end": v(-244.9, -85.9) * mm, "construction": true});
            skCircle(sketch, "E5.0.0.6", {"center": v(-244.9, -5.9) * mm, "radius": 2 * mm});
            skCircle(sketch, "E5.0.0.7", {"center": v(-244.9, 10.1) * mm, "radius": 2 * mm});
            skCircle(sketch, "E5.0.0.8", {"center": v(-244.9, 26.1) * mm, "radius": 2 * mm});
            skCircle(sketch, "E5.0.0.9", {"center": v(-244.9, 42.1) * mm, "radius": 2 * mm});
            skCircle(sketch, "E5.0.1.6", {"center": v(-228.9, -5.9) * mm, "radius": 2 * mm});
            skCircle(sketch, "E5.0.1.7", {"center": v(-228.9, 10.1) * mm, "radius": 2 * mm});
            skCircle(sketch, "E5.0.1.8", {"center": v(-228.9, 26.1) * mm, "radius": 2 * mm});
            skCircle(sketch, "E5.0.1.9", {"center": v(-228.9, 42.1) * mm, "radius": 2 * mm});
            skCircle(sketch, "E5.0.2.6", {"center": v(-212.9, -5.9) * mm, "radius": 2 * mm});
            skCircle(sketch, "E5.0.2.7", {"center": v(-212.9, 10.1) * mm, "radius": 2 * mm});
            skCircle(sketch, "E5.0.2.8", {"center": v(-212.9, 26.1) * mm, "radius": 2 * mm});
            skCircle(sketch, "E5.0.2.9", {"center": v(-212.9, 42.1) * mm, "radius": 2 * mm});
            skCircle(sketch, "E5.0.3.6", {"center": v(-196.9, -5.9) * mm, "radius": 2 * mm});
            skCircle(sketch, "E5.0.3.7", {"center": v(-196.9, 10.1) * mm, "radius": 2 * mm});
            skCircle(sketch, "E5.0.3.8", {"center": v(-196.9, 26.1) * mm, "radius": 2 * mm});
            skCircle(sketch, "E5.0.3.9", {"center": v(-196.9, 42.1) * mm, "radius": 2 * mm});
            skCircle(sketch, "E5.0.4.6", {"center": v(-180.9, -5.9) * mm, "radius": 2 * mm});
            skCircle(sketch, "E5.0.4.7", {"center": v(-180.9, 10.1) * mm, "radius": 2 * mm});
            skCircle(sketch, "E5.0.4.8", {"center": v(-180.9, 26.1) * mm, "radius": 2 * mm});
            skCircle(sketch, "E5.0.4.9", {"center": v(-180.9, 42.1) * mm, "radius": 2 * mm});
            skCircle(sketch, "E5.0.5.6", {"center": v(-164.9, -5.9) * mm, "radius": 2 * mm});
            skCircle(sketch, "E5.0.5.7", {"center": v(-164.9, 10.1) * mm, "radius": 2 * mm});
            skCircle(sketch, "E5.0.5.8", {"center": v(-164.9, 26.1) * mm, "radius": 2 * mm});
            skCircle(sketch, "E5.0.5.9", {"center": v(-164.9, 42.1) * mm, "radius": 2 * mm});
            skCircle(sketch, "E5.0.6.6", {"center": v(-148.9, -5.9) * mm, "radius": 2 * mm});
            skCircle(sketch, "E5.0.6.7", {"center": v(-148.9, 10.1) * mm, "radius": 2 * mm});
            skCircle(sketch, "E5.0.6.8", {"center": v(-148.9, 26.1) * mm, "radius": 2 * mm});
            skCircle(sketch, "E5.0.6.9", {"center": v(-148.9, 42.1) * mm, "radius": 2 * mm});
            skCircle(sketch, "E5.0.7.6", {"center": v(-132.9, -5.9) * mm, "radius": 2 * mm});
            skCircle(sketch, "E5.0.7.7", {"center": v(-132.9, 10.1) * mm, "radius": 2 * mm});
            skCircle(sketch, "E5.0.7.8", {"center": v(-132.9, 26.1) * mm, "radius": 2 * mm});
            skCircle(sketch, "E5.0.7.9", {"center": v(-132.9, 42.1) * mm, "radius": 2 * mm});
            skCircle(sketch, "E5.0.8.6", {"center": v(-116.9, -5.9) * mm, "radius": 2 * mm});
            skCircle(sketch, "E5.0.8.7", {"center": v(-116.9, 10.1) * mm, "radius": 2 * mm});
            skCircle(sketch, "E5.0.8.8", {"center": v(-116.9, 26.1) * mm, "radius": 2 * mm});
            skCircle(sketch, "E5.0.8.9", {"center": v(-116.9, 42.1) * mm, "radius": 2 * mm});
            skCircle(sketch, "E5.0.9.6", {"center": v(-100.9, -5.9) * mm, "radius": 2 * mm});
            skCircle(sketch, "E5.0.9.7", {"center": v(-100.9, 10.1) * mm, "radius": 2 * mm});
            skCircle(sketch, "E5.0.9.8", {"center": v(-100.9, 26.1) * mm, "radius": 2 * mm});
            skCircle(sketch, "E5.0.9.9", {"center": v(-100.9, 42.1) * mm, "radius": 2 * mm});
            skCircle(sketch, "E5.0.10.6", {"center": v(-84.9, -5.9) * mm, "radius": 2 * mm});
            skCircle(sketch, "E5.0.10.7", {"center": v(-84.9, 10.1) * mm, "radius": 2 * mm});
            skCircle(sketch, "E5.0.10.8", {"center": v(-84.9, 26.1) * mm, "radius": 2 * mm});
            skCircle(sketch, "E5.0.10.9", {"center": v(-84.9, 42.1) * mm, "radius": 2 * mm});
            skCircle(sketch, "E5.0.11.6", {"center": v(-68.9, -5.9) * mm, "radius": 2 * mm});
            skCircle(sketch, "E5.0.11.7", {"center": v(-68.9, 10.1) * mm, "radius": 2 * mm});
            skCircle(sketch, "E5.0.11.8", {"center": v(-68.9, 26.1) * mm, "radius": 2 * mm});
            skCircle(sketch, "E5.0.11.9", {"center": v(-68.9, 42.1) * mm, "radius": 2 * mm});
            skCircle(sketch, "E5.0.12.6", {"center": v(-52.9, -5.9) * mm, "radius": 2 * mm});
            skCircle(sketch, "E5.0.12.7", {"center": v(-52.9, 10.1) * mm, "radius": 2 * mm});
            skCircle(sketch, "E5.0.12.8", {"center": v(-52.9, 26.1) * mm, "radius": 2 * mm});
            skCircle(sketch, "E5.0.12.9", {"center": v(-52.9, 42.1) * mm, "radius": 2 * mm});
            skCircle(sketch, "E5.0.13.6", {"center": v(-36.9, -5.9) * mm, "radius": 2 * mm});
            skCircle(sketch, "E5.0.13.7", {"center": v(-36.9, 10.1) * mm, "radius": 2 * mm});
            skCircle(sketch, "E5.0.13.8", {"center": v(-36.9, 26.1) * mm, "radius": 2 * mm});
            skCircle(sketch, "E5.0.13.9", {"center": v(-36.9, 42.1) * mm, "radius": 2 * mm});
            skCircle(sketch, "E5.0.14.6", {"center": v(-20.9, -5.9) * mm, "radius": 2 * mm});
            skCircle(sketch, "E5.0.14.7", {"center": v(-20.9, 10.1) * mm, "radius": 2 * mm});
            skCircle(sketch, "E5.0.14.8", {"center": v(-20.9, 26.1) * mm, "radius": 2 * mm});
            skCircle(sketch, "E5.0.14.9", {"center": v(-20.9, 42.1) * mm, "radius": 2 * mm});
            skCircle(sketch, "E5.0.15.6", {"center": v(-4.9, -5.9) * mm, "radius": 2 * mm});
            skCircle(sketch, "E5.0.15.7", {"center": v(-4.9, 10.1) * mm, "radius": 2 * mm});
            skCircle(sketch, "E5.0.15.8", {"center": v(-4.9, 26.1) * mm, "radius": 2 * mm});
            skCircle(sketch, "E5.0.15.9", {"center": v(-4.9, 42.1) * mm, "radius": 2 * mm});
            skCircle(sketch, "E5.0.16.6", {"center": v(11.1, -5.9) * mm, "radius": 2 * mm});
            skCircle(sketch, "E5.0.16.7", {"center": v(11.1, 10.1) * mm, "radius": 2 * mm});
            skCircle(sketch, "E5.0.16.8", {"center": v(11.1, 26.1) * mm, "radius": 2 * mm});
            skCircle(sketch, "E5.0.16.9", {"center": v(11.1, 42.1) * mm, "radius": 2 * mm});
            skCircle(sketch, "E5.0.17.6", {"center": v(27.1, -5.9) * mm, "radius": 2 * mm});
            skCircle(sketch, "E5.0.17.7", {"center": v(27.1, 10.1) * mm, "radius": 2 * mm});
            skCircle(sketch, "E5.0.17.8", {"center": v(27.1, 26.1) * mm, "radius": 2 * mm});
            skCircle(sketch, "E5.0.17.9", {"center": v(27.1, 42.1) * mm, "radius": 2 * mm});
            skCircle(sketch, "E5.0.18.6", {"center": v(43.1, -5.9) * mm, "radius": 2 * mm});
            skCircle(sketch, "E5.0.18.7", {"center": v(43.1, 10.1) * mm, "radius": 2 * mm});
            skCircle(sketch, "E5.0.18.8", {"center": v(43.1, 26.1) * mm, "radius": 2 * mm});
            skCircle(sketch, "E5.0.18.9", {"center": v(43.1, 42.1) * mm, "radius": 2 * mm});
            skCircle(sketch, "E5.0.19.6", {"center": v(59.1, -5.9) * mm, "radius": 2 * mm});
            skCircle(sketch, "E5.0.19.7", {"center": v(59.1, 10.1) * mm, "radius": 2 * mm});
            skCircle(sketch, "E5.0.19.8", {"center": v(59.1, 26.1) * mm, "radius": 2 * mm});
            skCircle(sketch, "E5.0.19.9", {"center": v(59.1, 42.1) * mm, "radius": 2 * mm});
            skCircle(sketch, "E5.0.20.6", {"center": v(75.1, -5.9) * mm, "radius": 2 * mm});
            skCircle(sketch, "E5.0.20.7", {"center": v(75.1, 10.1) * mm, "radius": 2 * mm});
            skCircle(sketch, "E5.0.20.8", {"center": v(75.1, 26.1) * mm, "radius": 2 * mm});
            skCircle(sketch, "E5.0.20.9", {"center": v(75.1, 42.1) * mm, "radius": 2 * mm});
            skCircle(sketch, "E5.0.21.6", {"center": v(91.1, -5.9) * mm, "radius": 2 * mm});
            skCircle(sketch, "E5.0.21.7", {"center": v(91.1, 10.1) * mm, "radius": 2 * mm});
            skCircle(sketch, "E5.0.21.8", {"center": v(91.1, 26.1) * mm, "radius": 2 * mm});
            skCircle(sketch, "E5.0.21.9", {"center": v(91.1, 42.1) * mm, "radius": 2 * mm});
            skCircle(sketch, "E5.0.22.6", {"center": v(107.1, -5.9) * mm, "radius": 2 * mm});
            skCircle(sketch, "E5.0.22.7", {"center": v(107.1, 10.1) * mm, "radius": 2 * mm});
            skCircle(sketch, "E5.0.22.8", {"center": v(107.1, 26.1) * mm, "radius": 2 * mm});
            skCircle(sketch, "E5.0.22.9", {"center": v(107.1, 42.1) * mm, "radius": 2 * mm});
            skCircle(sketch, "E5.0.23.6", {"center": v(123.1, -5.9) * mm, "radius": 2 * mm});
            skCircle(sketch, "E5.0.23.7", {"center": v(123.1, 10.1) * mm, "radius": 2 * mm});
            skCircle(sketch, "E5.0.23.8", {"center": v(123.1, 26.1) * mm, "radius": 2 * mm});
            skCircle(sketch, "E5.0.23.9", {"center": v(123.1, 42.1) * mm, "radius": 2 * mm});
            skCircle(sketch, "E5.0.24.6", {"center": v(139.1, -5.9) * mm, "radius": 2 * mm});
            skCircle(sketch, "E5.0.24.7", {"center": v(139.1, 10.1) * mm, "radius": 2 * mm});
            skCircle(sketch, "E5.0.24.8", {"center": v(139.1, 26.1) * mm, "radius": 2 * mm});
            skCircle(sketch, "E5.0.24.9", {"center": v(139.1, 42.1) * mm, "radius": 2 * mm});
            skCircle(sketch, "E5.0.25.6", {"center": v(155.1, -5.9) * mm, "radius": 2 * mm});
            skCircle(sketch, "E5.0.25.7", {"center": v(155.1, 10.1) * mm, "radius": 2 * mm});
            skCircle(sketch, "E5.0.25.8", {"center": v(155.1, 26.1) * mm, "radius": 2 * mm});
            skCircle(sketch, "E5.0.25.9", {"center": v(155.1, 42.1) * mm, "radius": 2 * mm});
            skCircle(sketch, "E5.0.26.6", {"center": v(171.1, -5.9) * mm, "radius": 2 * mm});
            skCircle(sketch, "E5.0.26.7", {"center": v(171.1, 10.1) * mm, "radius": 2 * mm});
            skCircle(sketch, "E5.0.26.8", {"center": v(171.1, 26.1) * mm, "radius": 2 * mm});
            skCircle(sketch, "E5.0.26.9", {"center": v(171.1, 42.1) * mm, "radius": 2 * mm});
            skCircle(sketch, "E5.0.27.6", {"center": v(187.1, -5.9) * mm, "radius": 2 * mm});
            skCircle(sketch, "E5.0.27.7", {"center": v(187.1, 10.1) * mm, "radius": 2 * mm});
            skCircle(sketch, "E5.0.27.8", {"center": v(187.1, 26.1) * mm, "radius": 2 * mm});
            skCircle(sketch, "E5.0.27.9", {"center": v(187.1, 42.1) * mm, "radius": 2 * mm});
            skCircle(sketch, "E5.0.28.6", {"center": v(203.1, -5.9) * mm, "radius": 2 * mm});
            skCircle(sketch, "E5.0.28.7", {"center": v(203.1, 10.1) * mm, "radius": 2 * mm});
            skCircle(sketch, "E5.0.28.8", {"center": v(203.1, 26.1) * mm, "radius": 2 * mm});
            skCircle(sketch, "E5.0.28.9", {"center": v(203.1, 42.1) * mm, "radius": 2 * mm});
            skCircle(sketch, "E5.0.29.6", {"center": v(219.1, -5.9) * mm, "radius": 2 * mm});
            skCircle(sketch, "E5.0.29.7", {"center": v(219.1, 10.1) * mm, "radius": 2 * mm});
            skCircle(sketch, "E5.0.29.8", {"center": v(219.1, 26.1) * mm, "radius": 2 * mm});
            skCircle(sketch, "E5.0.29.9", {"center": v(219.1, 42.1) * mm, "radius": 2 * mm});
            skCircle(sketch, "E5.0.30.6", {"center": v(235.1, -5.9) * mm, "radius": 2 * mm});
            skCircle(sketch, "E5.0.30.7", {"center": v(235.1, 10.1) * mm, "radius": 2 * mm});
            skCircle(sketch, "E5.0.30.8", {"center": v(235.1, 26.1) * mm, "radius": 2 * mm});
            skCircle(sketch, "E5.0.30.9", {"center": v(235.1, 42.1) * mm, "radius": 2 * mm});
            skCircle(sketch, "E6.0.0.8", {"center": v(-252.9, 18.1) * mm, "radius": 2 * mm});
            skCircle(sketch, "E6.0.0.9", {"center": v(-252.9, 34.1) * mm, "radius": 2 * mm});
            skCircle(sketch, "E6.0.1.8", {"center": v(-236.9, 18.1) * mm, "radius": 2 * mm});
            skCircle(sketch, "E6.0.1.9", {"center": v(-236.9, 34.1) * mm, "radius": 2 * mm});
            skCircle(sketch, "E6.0.2.8", {"center": v(-220.9, 18.1) * mm, "radius": 2 * mm});
            skCircle(sketch, "E6.0.2.9", {"center": v(-220.9, 34.1) * mm, "radius": 2 * mm});
            skCircle(sketch, "E6.0.3.8", {"center": v(-204.9, 18.1) * mm, "radius": 2 * mm});
            skCircle(sketch, "E6.0.3.9", {"center": v(-204.9, 34.1) * mm, "radius": 2 * mm});
            skCircle(sketch, "E6.0.4.8", {"center": v(-188.9, 18.1) * mm, "radius": 2 * mm});
            skCircle(sketch, "E6.0.4.9", {"center": v(-188.9, 34.1) * mm, "radius": 2 * mm});
            skCircle(sketch, "E6.0.5.8", {"center": v(-172.9, 18.1) * mm, "radius": 2 * mm});
            skCircle(sketch, "E6.0.5.9", {"center": v(-172.9, 34.1) * mm, "radius": 2 * mm});
            skCircle(sketch, "E6.0.6.8", {"center": v(-156.9, 18.1) * mm, "radius": 2 * mm});
            skCircle(sketch, "E6.0.6.9", {"center": v(-156.9, 34.1) * mm, "radius": 2 * mm});
            skCircle(sketch, "E6.0.7.8", {"center": v(-140.9, 18.1) * mm, "radius": 2 * mm});
            skCircle(sketch, "E6.0.7.9", {"center": v(-140.9, 34.1) * mm, "radius": 2 * mm});
            skCircle(sketch, "E6.0.8.8", {"center": v(-124.9, 18.1) * mm, "radius": 2 * mm});
            skCircle(sketch, "E6.0.8.9", {"center": v(-124.9, 34.1) * mm, "radius": 2 * mm});
            skCircle(sketch, "E6.0.9.8", {"center": v(-108.9, 18.1) * mm, "radius": 2 * mm});
            skCircle(sketch, "E6.0.9.9", {"center": v(-108.9, 34.1) * mm, "radius": 2 * mm});
            skCircle(sketch, "E6.0.10.8", {"center": v(-92.9, 18.1) * mm, "radius": 2 * mm});
            skCircle(sketch, "E6.0.10.9", {"center": v(-92.9, 34.1) * mm, "radius": 2 * mm});
            skCircle(sketch, "E6.0.11.8", {"center": v(-76.9, 18.1) * mm, "radius": 2 * mm});
            skCircle(sketch, "E6.0.11.9", {"center": v(-76.9, 34.1) * mm, "radius": 2 * mm});
            skCircle(sketch, "E6.0.12.8", {"center": v(-60.9, 18.1) * mm, "radius": 2 * mm});
            skCircle(sketch, "E6.0.12.9", {"center": v(-60.9, 34.1) * mm, "radius": 2 * mm});
            skCircle(sketch, "E6.0.13.8", {"center": v(-44.9, 18.1) * mm, "radius": 2 * mm});
            skCircle(sketch, "E6.0.13.9", {"center": v(-44.9, 34.1) * mm, "radius": 2 * mm});
            skCircle(sketch, "E6.0.14.8", {"center": v(-28.9, 18.1) * mm, "radius": 2 * mm});
            skCircle(sketch, "E6.0.14.9", {"center": v(-28.9, 34.1) * mm, "radius": 2 * mm});
            skCircle(sketch, "E6.0.15.8", {"center": v(-12.9, 18.1) * mm, "radius": 2 * mm});
            skCircle(sketch, "E6.0.15.9", {"center": v(-12.9, 34.1) * mm, "radius": 2 * mm});
            skCircle(sketch, "E6.0.16.8", {"center": v(3.1, 18.1) * mm, "radius": 2 * mm});
            skCircle(sketch, "E6.0.16.9", {"center": v(3.1, 34.1) * mm, "radius": 2 * mm});
            skCircle(sketch, "E6.0.17.8", {"center": v(19.1, 18.1) * mm, "radius": 2 * mm});
            skCircle(sketch, "E6.0.17.9", {"center": v(19.1, 34.1) * mm, "radius": 2 * mm});
            skCircle(sketch, "E6.0.18.8", {"center": v(35.1, 18.1) * mm, "radius": 2 * mm});
            skCircle(sketch, "E6.0.18.9", {"center": v(35.1, 34.1) * mm, "radius": 2 * mm});
            skCircle(sketch, "E6.0.19.8", {"center": v(51.1, 18.1) * mm, "radius": 2 * mm});
            skCircle(sketch, "E6.0.19.9", {"center": v(51.1, 34.1) * mm, "radius": 2 * mm});
            skCircle(sketch, "E6.0.20.8", {"center": v(67.1, 18.1) * mm, "radius": 2 * mm});
            skCircle(sketch, "E6.0.20.9", {"center": v(67.1, 34.1) * mm, "radius": 2 * mm});
            skCircle(sketch, "E6.0.21.8", {"center": v(83.1, 18.1) * mm, "radius": 2 * mm});
            skCircle(sketch, "E6.0.21.9", {"center": v(83.1, 34.1) * mm, "radius": 2 * mm});
            skCircle(sketch, "E6.0.22.8", {"center": v(99.1, 18.1) * mm, "radius": 2 * mm});
            skCircle(sketch, "E6.0.22.9", {"center": v(99.1, 34.1) * mm, "radius": 2 * mm});
            skCircle(sketch, "E6.0.23.8", {"center": v(115.1, 18.1) * mm, "radius": 2 * mm});
            skCircle(sketch, "E6.0.23.9", {"center": v(115.1, 34.1) * mm, "radius": 2 * mm});
            skCircle(sketch, "E6.0.24.8", {"center": v(131.1, 18.1) * mm, "radius": 2 * mm});
            skCircle(sketch, "E6.0.24.9", {"center": v(131.1, 34.1) * mm, "radius": 2 * mm});
            skCircle(sketch, "E6.0.25.8", {"center": v(147.1, 18.1) * mm, "radius": 2 * mm});
            skCircle(sketch, "E6.0.25.9", {"center": v(147.1, 34.1) * mm, "radius": 2 * mm});
            skCircle(sketch, "E6.0.26.8", {"center": v(163.1, 18.1) * mm, "radius": 2 * mm});
            skCircle(sketch, "E6.0.26.9", {"center": v(163.1, 34.1) * mm, "radius": 2 * mm});
            skCircle(sketch, "E6.0.27.8", {"center": v(179.1, 18.1) * mm, "radius": 2 * mm});
            skCircle(sketch, "E6.0.27.9", {"center": v(179.1, 34.1) * mm, "radius": 2 * mm});
            skCircle(sketch, "E6.0.28.8", {"center": v(195.1, 18.1) * mm, "radius": 2 * mm});
            skCircle(sketch, "E6.0.28.9", {"center": v(195.1, 34.1) * mm, "radius": 2 * mm});
            skCircle(sketch, "E6.0.29.8", {"center": v(211.1, 18.1) * mm, "radius": 2 * mm});
            skCircle(sketch, "E6.0.29.9", {"center": v(211.1, 34.1) * mm, "radius": 2 * mm});
            skCircle(sketch, "E6.0.30.8", {"center": v(227.1, 18.1) * mm, "radius": 2 * mm});
            skCircle(sketch, "E6.0.30.9", {"center": v(227.1, 34.1) * mm, "radius": 2 * mm});
            skCircle(sketch, "E7.0.0.10", {"center": v(-252.9, 50.1) * mm, "radius": 2 * mm});
            skCircle(sketch, "E7.0.0.11", {"center": v(-252.9, 66.1) * mm, "radius": 2 * mm});
            skCircle(sketch, "E7.0.0.12", {"center": v(-252.9, 82.1) * mm, "radius": 2 * mm});
            skCircle(sketch, "E7.0.1.10", {"center": v(-236.9, 50.1) * mm, "radius": 2 * mm});
            skCircle(sketch, "E7.0.1.11", {"center": v(-236.9, 66.1) * mm, "radius": 2 * mm});
            skCircle(sketch, "E7.0.1.12", {"center": v(-236.9, 82.1) * mm, "radius": 2 * mm});
            skCircle(sketch, "E7.0.2.10", {"center": v(-220.9, 50.1) * mm, "radius": 2 * mm});
            skCircle(sketch, "E7.0.2.11", {"center": v(-220.9, 66.1) * mm, "radius": 2 * mm});
            skCircle(sketch, "E7.0.2.12", {"center": v(-220.9, 82.1) * mm, "radius": 2 * mm});
            skCircle(sketch, "E7.0.3.10", {"center": v(-204.9, 50.1) * mm, "radius": 2 * mm});
            skCircle(sketch, "E7.0.3.11", {"center": v(-204.9, 66.1) * mm, "radius": 2 * mm});
            skCircle(sketch, "E7.0.3.12", {"center": v(-204.9, 82.1) * mm, "radius": 2 * mm});
            skCircle(sketch, "E7.0.4.10", {"center": v(-188.9, 50.1) * mm, "radius": 2 * mm});
            skCircle(sketch, "E7.0.4.11", {"center": v(-188.9, 66.1) * mm, "radius": 2 * mm});
            skCircle(sketch, "E7.0.4.12", {"center": v(-188.9, 82.1) * mm, "radius": 2 * mm});
            skCircle(sketch, "E7.0.5.10", {"center": v(-172.9, 50.1) * mm, "radius": 2 * mm});
            skCircle(sketch, "E7.0.5.11", {"center": v(-172.9, 66.1) * mm, "radius": 2 * mm});
            skCircle(sketch, "E7.0.5.12", {"center": v(-172.9, 82.1) * mm, "radius": 2 * mm});
            skCircle(sketch, "E7.0.6.10", {"center": v(-156.9, 50.1) * mm, "radius": 2 * mm});
            skCircle(sketch, "E7.0.6.11", {"center": v(-156.9, 66.1) * mm, "radius": 2 * mm});
            skCircle(sketch, "E7.0.6.12", {"center": v(-156.9, 82.1) * mm, "radius": 2 * mm});
            skCircle(sketch, "E7.0.7.10", {"center": v(-140.9, 50.1) * mm, "radius": 2 * mm});
            skCircle(sketch, "E7.0.7.11", {"center": v(-140.9, 66.1) * mm, "radius": 2 * mm});
            skCircle(sketch, "E7.0.7.12", {"center": v(-140.9, 82.1) * mm, "radius": 2 * mm});
            skCircle(sketch, "E7.0.8.10", {"center": v(-124.9, 50.1) * mm, "radius": 2 * mm});
            skCircle(sketch, "E7.0.8.11", {"center": v(-124.9, 66.1) * mm, "radius": 2 * mm});
            skCircle(sketch, "E7.0.8.12", {"center": v(-124.9, 82.1) * mm, "radius": 2 * mm});
            skCircle(sketch, "E7.0.9.10", {"center": v(-108.9, 50.1) * mm, "radius": 2 * mm});
            skCircle(sketch, "E7.0.9.11", {"center": v(-108.9, 66.1) * mm, "radius": 2 * mm});
            skCircle(sketch, "E7.0.9.12", {"center": v(-108.9, 82.1) * mm, "radius": 2 * mm});
            skCircle(sketch, "E7.0.10.10", {"center": v(-92.9, 50.1) * mm, "radius": 2 * mm});
            skCircle(sketch, "E7.0.10.11", {"center": v(-92.9, 66.1) * mm, "radius": 2 * mm});
            skCircle(sketch, "E7.0.10.12", {"center": v(-92.9, 82.1) * mm, "radius": 2 * mm});
            skCircle(sketch, "E7.0.11.10", {"center": v(-76.9, 50.1) * mm, "radius": 2 * mm});
            skCircle(sketch, "E7.0.11.11", {"center": v(-76.9, 66.1) * mm, "radius": 2 * mm});
            skCircle(sketch, "E7.0.11.12", {"center": v(-76.9, 82.1) * mm, "radius": 2 * mm});
            skCircle(sketch, "E7.0.12.10", {"center": v(-60.9, 50.1) * mm, "radius": 2 * mm});
            skCircle(sketch, "E7.0.12.11", {"center": v(-60.9, 66.1) * mm, "radius": 2 * mm});
            skCircle(sketch, "E7.0.12.12", {"center": v(-60.9, 82.1) * mm, "radius": 2 * mm});
            skCircle(sketch, "E7.0.13.10", {"center": v(-44.9, 50.1) * mm, "radius": 2 * mm});
            skCircle(sketch, "E7.0.13.11", {"center": v(-44.9, 66.1) * mm, "radius": 2 * mm});
            skCircle(sketch, "E7.0.13.12", {"center": v(-44.9, 82.1) * mm, "radius": 2 * mm});
            skCircle(sketch, "E7.0.14.10", {"center": v(-28.9, 50.1) * mm, "radius": 2 * mm});
            skCircle(sketch, "E7.0.14.11", {"center": v(-28.9, 66.1) * mm, "radius": 2 * mm});
            skCircle(sketch, "E7.0.14.12", {"center": v(-28.9, 82.1) * mm, "radius": 2 * mm});
            skCircle(sketch, "E7.0.15.10", {"center": v(-12.9, 50.1) * mm, "radius": 2 * mm});
            skCircle(sketch, "E7.0.15.11", {"center": v(-12.9, 66.1) * mm, "radius": 2 * mm});
            skCircle(sketch, "E7.0.15.12", {"center": v(-12.9, 82.1) * mm, "radius": 2 * mm});
            skCircle(sketch, "E7.0.16.10", {"center": v(3.1, 50.1) * mm, "radius": 2 * mm});
            skCircle(sketch, "E7.0.16.11", {"center": v(3.1, 66.1) * mm, "radius": 2 * mm});
            skCircle(sketch, "E7.0.16.12", {"center": v(3.1, 82.1) * mm, "radius": 2 * mm});
            skCircle(sketch, "E7.0.17.10", {"center": v(19.1, 50.1) * mm, "radius": 2 * mm});
            skCircle(sketch, "E7.0.17.11", {"center": v(19.1, 66.1) * mm, "radius": 2 * mm});
            skCircle(sketch, "E7.0.17.12", {"center": v(19.1, 82.1) * mm, "radius": 2 * mm});
            skCircle(sketch, "E7.0.18.10", {"center": v(35.1, 50.1) * mm, "radius": 2 * mm});
            skCircle(sketch, "E7.0.18.11", {"center": v(35.1, 66.1) * mm, "radius": 2 * mm});
            skCircle(sketch, "E7.0.18.12", {"center": v(35.1, 82.1) * mm, "radius": 2 * mm});
            skCircle(sketch, "E7.0.19.10", {"center": v(51.1, 50.1) * mm, "radius": 2 * mm});
            skCircle(sketch, "E7.0.19.11", {"center": v(51.1, 66.1) * mm, "radius": 2 * mm});
            skCircle(sketch, "E7.0.19.12", {"center": v(51.1, 82.1) * mm, "radius": 2 * mm});
            skCircle(sketch, "E7.0.20.10", {"center": v(67.1, 50.1) * mm, "radius": 2 * mm});
            skCircle(sketch, "E7.0.20.11", {"center": v(67.1, 66.1) * mm, "radius": 2 * mm});
            skCircle(sketch, "E7.0.20.12", {"center": v(67.1, 82.1) * mm, "radius": 2 * mm});
            skCircle(sketch, "E7.0.21.10", {"center": v(83.1, 50.1) * mm, "radius": 2 * mm});
            skCircle(sketch, "E7.0.21.11", {"center": v(83.1, 66.1) * mm, "radius": 2 * mm});
            skCircle(sketch, "E7.0.21.12", {"center": v(83.1, 82.1) * mm, "radius": 2 * mm});
            skCircle(sketch, "E7.0.22.10", {"center": v(99.1, 50.1) * mm, "radius": 2 * mm});
            skCircle(sketch, "E7.0.22.11", {"center": v(99.1, 66.1) * mm, "radius": 2 * mm});
            skCircle(sketch, "E7.0.22.12", {"center": v(99.1, 82.1) * mm, "radius": 2 * mm});
            skCircle(sketch, "E7.0.23.10", {"center": v(115.1, 50.1) * mm, "radius": 2 * mm});
            skCircle(sketch, "E7.0.23.11", {"center": v(115.1, 66.1) * mm, "radius": 2 * mm});
            skCircle(sketch, "E7.0.23.12", {"center": v(115.1, 82.1) * mm, "radius": 2 * mm});
            skCircle(sketch, "E7.0.24.10", {"center": v(131.1, 50.1) * mm, "radius": 2 * mm});
            skCircle(sketch, "E7.0.24.11", {"center": v(131.1, 66.1) * mm, "radius": 2 * mm});
            skCircle(sketch, "E7.0.24.12", {"center": v(131.1, 82.1) * mm, "radius": 2 * mm});
            skCircle(sketch, "E7.0.25.10", {"center": v(147.1, 50.1) * mm, "radius": 2 * mm});
            skCircle(sketch, "E7.0.25.11", {"center": v(147.1, 66.1) * mm, "radius": 2 * mm});
            skCircle(sketch, "E7.0.25.12", {"center": v(147.1, 82.1) * mm, "radius": 2 * mm});
            skCircle(sketch, "E7.0.26.10", {"center": v(163.1, 50.1) * mm, "radius": 2 * mm});
            skCircle(sketch, "E7.0.26.11", {"center": v(163.1, 66.1) * mm, "radius": 2 * mm});
            skCircle(sketch, "E7.0.26.12", {"center": v(163.1, 82.1) * mm, "radius": 2 * mm});
            skCircle(sketch, "E7.0.27.10", {"center": v(179.1, 50.1) * mm, "radius": 2 * mm});
            skCircle(sketch, "E7.0.27.11", {"center": v(179.1, 66.1) * mm, "radius": 2 * mm});
            skCircle(sketch, "E7.0.27.12", {"center": v(179.1, 82.1) * mm, "radius": 2 * mm});
            skCircle(sketch, "E7.0.28.10", {"center": v(195.1, 50.1) * mm, "radius": 2 * mm});
            skCircle(sketch, "E7.0.28.11", {"center": v(195.1, 66.1) * mm, "radius": 2 * mm});
            skCircle(sketch, "E7.0.28.12", {"center": v(195.1, 82.1) * mm, "radius": 2 * mm});
            skCircle(sketch, "E7.0.29.10", {"center": v(211.1, 50.1) * mm, "radius": 2 * mm});
            skCircle(sketch, "E7.0.29.11", {"center": v(211.1, 66.1) * mm, "radius": 2 * mm});
            skCircle(sketch, "E7.0.29.12", {"center": v(211.1, 82.1) * mm, "radius": 2 * mm});
            skCircle(sketch, "E7.0.30.10", {"center": v(227.1, 50.1) * mm, "radius": 2 * mm});
            skCircle(sketch, "E7.0.30.11", {"center": v(227.1, 66.1) * mm, "radius": 2 * mm});
            skCircle(sketch, "E7.0.30.12", {"center": v(227.1, 82.1) * mm, "radius": 2 * mm});
            skCircle(sketch, "E8.0.0.10", {"center": v(-244.9, 58.1) * mm, "radius": 2 * mm});
            skCircle(sketch, "E8.0.0.11", {"center": v(-244.9, 74.1) * mm, "radius": 2 * mm});
            skCircle(sketch, "E8.0.0.12", {"center": v(-244.9, 90.1) * mm, "radius": 2 * mm});
            skCircle(sketch, "E8.0.1.10", {"center": v(-228.9, 58.1) * mm, "radius": 2 * mm});
            skCircle(sketch, "E8.0.1.11", {"center": v(-228.9, 74.1) * mm, "radius": 2 * mm});
            skCircle(sketch, "E8.0.1.12", {"center": v(-228.9, 90.1) * mm, "radius": 2 * mm});
            skCircle(sketch, "E8.0.2.10", {"center": v(-212.9, 58.1) * mm, "radius": 2 * mm});
            skCircle(sketch, "E8.0.2.11", {"center": v(-212.9, 74.1) * mm, "radius": 2 * mm});
            skCircle(sketch, "E8.0.2.12", {"center": v(-212.9, 90.1) * mm, "radius": 2 * mm});
            skCircle(sketch, "E8.0.3.10", {"center": v(-196.9, 58.1) * mm, "radius": 2 * mm});
            skCircle(sketch, "E8.0.3.11", {"center": v(-196.9, 74.1) * mm, "radius": 2 * mm});
            skCircle(sketch, "E8.0.3.12", {"center": v(-196.9, 90.1) * mm, "radius": 2 * mm});
            skCircle(sketch, "E8.0.4.10", {"center": v(-180.9, 58.1) * mm, "radius": 2 * mm});
            skCircle(sketch, "E8.0.4.11", {"center": v(-180.9, 74.1) * mm, "radius": 2 * mm});
            skCircle(sketch, "E8.0.4.12", {"center": v(-180.9, 90.1) * mm, "radius": 2 * mm});
            skCircle(sketch, "E8.0.5.10", {"center": v(-164.9, 58.1) * mm, "radius": 2 * mm});
            skCircle(sketch, "E8.0.5.11", {"center": v(-164.9, 74.1) * mm, "radius": 2 * mm});
            skCircle(sketch, "E8.0.5.12", {"center": v(-164.9, 90.1) * mm, "radius": 2 * mm});
            skCircle(sketch, "E8.0.6.10", {"center": v(-148.9, 58.1) * mm, "radius": 2 * mm});
            skCircle(sketch, "E8.0.6.11", {"center": v(-148.9, 74.1) * mm, "radius": 2 * mm});
            skCircle(sketch, "E8.0.6.12", {"center": v(-148.9, 90.1) * mm, "radius": 2 * mm});
            skCircle(sketch, "E8.0.7.10", {"center": v(-132.9, 58.1) * mm, "radius": 2 * mm});
            skCircle(sketch, "E8.0.7.11", {"center": v(-132.9, 74.1) * mm, "radius": 2 * mm});
            skCircle(sketch, "E8.0.7.12", {"center": v(-132.9, 90.1) * mm, "radius": 2 * mm});
            skCircle(sketch, "E8.0.8.10", {"center": v(-116.9, 58.1) * mm, "radius": 2 * mm});
            skCircle(sketch, "E8.0.8.11", {"center": v(-116.9, 74.1) * mm, "radius": 2 * mm});
            skCircle(sketch, "E8.0.8.12", {"center": v(-116.9, 90.1) * mm, "radius": 2 * mm});
            skCircle(sketch, "E8.0.9.10", {"center": v(-100.9, 58.1) * mm, "radius": 2 * mm});
            skCircle(sketch, "E8.0.9.11", {"center": v(-100.9, 74.1) * mm, "radius": 2 * mm});
            skCircle(sketch, "E8.0.9.12", {"center": v(-100.9, 90.1) * mm, "radius": 2 * mm});
            skCircle(sketch, "E8.0.10.10", {"center": v(-84.9, 58.1) * mm, "radius": 2 * mm});
            skCircle(sketch, "E8.0.10.11", {"center": v(-84.9, 74.1) * mm, "radius": 2 * mm});
            skCircle(sketch, "E8.0.10.12", {"center": v(-84.9, 90.1) * mm, "radius": 2 * mm});
            skCircle(sketch, "E8.0.11.10", {"center": v(-68.9, 58.1) * mm, "radius": 2 * mm});
            skCircle(sketch, "E8.0.11.11", {"center": v(-68.9, 74.1) * mm, "radius": 2 * mm});
            skCircle(sketch, "E8.0.11.12", {"center": v(-68.9, 90.1) * mm, "radius": 2 * mm});
            skCircle(sketch, "E8.0.12.10", {"center": v(-52.9, 58.1) * mm, "radius": 2 * mm});
            skCircle(sketch, "E8.0.12.11", {"center": v(-52.9, 74.1) * mm, "radius": 2 * mm});
            skCircle(sketch, "E8.0.12.12", {"center": v(-52.9, 90.1) * mm, "radius": 2 * mm});
            skCircle(sketch, "E8.0.13.10", {"center": v(-36.9, 58.1) * mm, "radius": 2 * mm});
            skCircle(sketch, "E8.0.13.11", {"center": v(-36.9, 74.1) * mm, "radius": 2 * mm});
            skCircle(sketch, "E8.0.13.12", {"center": v(-36.9, 90.1) * mm, "radius": 2 * mm});
            skCircle(sketch, "E8.0.14.10", {"center": v(-20.9, 58.1) * mm, "radius": 2 * mm});
            skCircle(sketch, "E8.0.14.11", {"center": v(-20.9, 74.1) * mm, "radius": 2 * mm});
            skCircle(sketch, "E8.0.14.12", {"center": v(-20.9, 90.1) * mm, "radius": 2 * mm});
            skCircle(sketch, "E8.0.15.10", {"center": v(-4.9, 58.1) * mm, "radius": 2 * mm});
            skCircle(sketch, "E8.0.15.11", {"center": v(-4.9, 74.1) * mm, "radius": 2 * mm});
            skCircle(sketch, "E8.0.15.12", {"center": v(-4.9, 90.1) * mm, "radius": 2 * mm});
            skCircle(sketch, "E8.0.16.10", {"center": v(11.1, 58.1) * mm, "radius": 2 * mm});
            skCircle(sketch, "E8.0.16.11", {"center": v(11.1, 74.1) * mm, "radius": 2 * mm});
            skCircle(sketch, "E8.0.16.12", {"center": v(11.1, 90.1) * mm, "radius": 2 * mm});
            skCircle(sketch, "E8.0.17.10", {"center": v(27.1, 58.1) * mm, "radius": 2 * mm});
            skCircle(sketch, "E8.0.17.11", {"center": v(27.1, 74.1) * mm, "radius": 2 * mm});
            skCircle(sketch, "E8.0.17.12", {"center": v(27.1, 90.1) * mm, "radius": 2 * mm});
            skCircle(sketch, "E8.0.18.10", {"center": v(43.1, 58.1) * mm, "radius": 2 * mm});
            skCircle(sketch, "E8.0.18.11", {"center": v(43.1, 74.1) * mm, "radius": 2 * mm});
            skCircle(sketch, "E8.0.18.12", {"center": v(43.1, 90.1) * mm, "radius": 2 * mm});
            skCircle(sketch, "E8.0.19.10", {"center": v(59.1, 58.1) * mm, "radius": 2 * mm});
            skCircle(sketch, "E8.0.19.11", {"center": v(59.1, 74.1) * mm, "radius": 2 * mm});
            skCircle(sketch, "E8.0.19.12", {"center": v(59.1, 90.1) * mm, "radius": 2 * mm});
            skCircle(sketch, "E8.0.20.10", {"center": v(75.1, 58.1) * mm, "radius": 2 * mm});
            skCircle(sketch, "E8.0.20.11", {"center": v(75.1, 74.1) * mm, "radius": 2 * mm});
            skCircle(sketch, "E8.0.20.12", {"center": v(75.1, 90.1) * mm, "radius": 2 * mm});
            skCircle(sketch, "E8.0.21.10", {"center": v(91.1, 58.1) * mm, "radius": 2 * mm});
            skCircle(sketch, "E8.0.21.11", {"center": v(91.1, 74.1) * mm, "radius": 2 * mm});
            skCircle(sketch, "E8.0.21.12", {"center": v(91.1, 90.1) * mm, "radius": 2 * mm});
            skCircle(sketch, "E8.0.22.10", {"center": v(107.1, 58.1) * mm, "radius": 2 * mm});
            skCircle(sketch, "E8.0.22.11", {"center": v(107.1, 74.1) * mm, "radius": 2 * mm});
            skCircle(sketch, "E8.0.22.12", {"center": v(107.1, 90.1) * mm, "radius": 2 * mm});
            skCircle(sketch, "E8.0.23.10", {"center": v(123.1, 58.1) * mm, "radius": 2 * mm});
            skCircle(sketch, "E8.0.23.11", {"center": v(123.1, 74.1) * mm, "radius": 2 * mm});
            skCircle(sketch, "E8.0.23.12", {"center": v(123.1, 90.1) * mm, "radius": 2 * mm});
            skCircle(sketch, "E8.0.24.10", {"center": v(139.1, 58.1) * mm, "radius": 2 * mm});
            skCircle(sketch, "E8.0.24.11", {"center": v(139.1, 74.1) * mm, "radius": 2 * mm});
            skCircle(sketch, "E8.0.24.12", {"center": v(139.1, 90.1) * mm, "radius": 2 * mm});
            skCircle(sketch, "E8.0.25.10", {"center": v(155.1, 58.1) * mm, "radius": 2 * mm});
            skCircle(sketch, "E8.0.25.11", {"center": v(155.1, 74.1) * mm, "radius": 2 * mm});
            skCircle(sketch, "E8.0.25.12", {"center": v(155.1, 90.1) * mm, "radius": 2 * mm});
            skCircle(sketch, "E8.0.26.10", {"center": v(171.1, 58.1) * mm, "radius": 2 * mm});
            skCircle(sketch, "E8.0.26.11", {"center": v(171.1, 74.1) * mm, "radius": 2 * mm});
            skCircle(sketch, "E8.0.26.12", {"center": v(171.1, 90.1) * mm, "radius": 2 * mm});
            skCircle(sketch, "E8.0.27.10", {"center": v(187.1, 58.1) * mm, "radius": 2 * mm});
            skCircle(sketch, "E8.0.27.11", {"center": v(187.1, 74.1) * mm, "radius": 2 * mm});
            skCircle(sketch, "E8.0.27.12", {"center": v(187.1, 90.1) * mm, "radius": 2 * mm});
            skCircle(sketch, "E8.0.28.10", {"center": v(203.1, 58.1) * mm, "radius": 2 * mm});
            skCircle(sketch, "E8.0.28.11", {"center": v(203.1, 74.1) * mm, "radius": 2 * mm});
            skCircle(sketch, "E8.0.28.12", {"center": v(203.1, 90.1) * mm, "radius": 2 * mm});
            skCircle(sketch, "E8.0.29.10", {"center": v(219.1, 58.1) * mm, "radius": 2 * mm});
            skCircle(sketch, "E8.0.29.11", {"center": v(219.1, 74.1) * mm, "radius": 2 * mm});
            skCircle(sketch, "E8.0.29.12", {"center": v(219.1, 90.1) * mm, "radius": 2 * mm});
            skCircle(sketch, "E8.0.30.10", {"center": v(235.1, 58.1) * mm, "radius": 2 * mm});
            skCircle(sketch, "E8.0.30.11", {"center": v(235.1, 74.1) * mm, "radius": 2 * mm});
            skCircle(sketch, "E8.0.30.12", {"center": v(235.1, 90.1) * mm, "radius": 2 * mm});
            skCircle(sketch, "E9.0.31.0", {"center": v(251.1, -101.9) * mm, "radius": 2 * mm});
            skCircle(sketch, "E9.0.31.1", {"center": v(251.1, -85.9) * mm, "radius": 2 * mm});
            skCircle(sketch, "E9.0.31.2", {"center": v(251.1, -69.9) * mm, "radius": 2 * mm});
            skCircle(sketch, "E9.0.31.3", {"center": v(251.1, -53.9) * mm, "radius": 2 * mm});
            skCircle(sketch, "E9.0.31.4", {"center": v(251.1, -37.9) * mm, "radius": 2 * mm});
            skCircle(sketch, "E9.0.31.5", {"center": v(251.1, -21.9) * mm, "radius": 2 * mm});
            skCircle(sketch, "E9.0.31.6", {"center": v(251.1, -5.9) * mm, "radius": 2 * mm});
            skCircle(sketch, "E9.0.31.7", {"center": v(251.1, 10.1) * mm, "radius": 2 * mm});
            skCircle(sketch, "E9.0.31.8", {"center": v(251.1, 26.1) * mm, "radius": 2 * mm});
            skCircle(sketch, "E9.0.31.9", {"center": v(251.1, 42.1) * mm, "radius": 2 * mm});
            skCircle(sketch, "E9.0.31.10", {"center": v(251.1, 58.1) * mm, "radius": 2 * mm});
            skCircle(sketch, "E9.0.31.11", {"center": v(251.1, 74.1) * mm, "radius": 2 * mm});
            skCircle(sketch, "E9.0.31.12", {"center": v(251.1, 90.1) * mm, "radius": 2 * mm});
            skCircle(sketch, "E9.0.32.0", {"center": v(267.1, -101.9) * mm, "radius": 2 * mm});
            skCircle(sketch, "E9.0.32.1", {"center": v(267.1, -85.9) * mm, "radius": 2 * mm});
            skCircle(sketch, "E9.0.32.2", {"center": v(267.1, -69.9) * mm, "radius": 2 * mm});
            skCircle(sketch, "E9.0.32.3", {"center": v(267.1, -53.9) * mm, "radius": 2 * mm});
            skCircle(sketch, "E9.0.32.4", {"center": v(267.1, -37.9) * mm, "radius": 2 * mm});
            skCircle(sketch, "E9.0.32.5", {"center": v(267.1, -21.9) * mm, "radius": 2 * mm});
            skCircle(sketch, "E9.0.32.6", {"center": v(267.1, -5.9) * mm, "radius": 2 * mm});
            skCircle(sketch, "E9.0.32.7", {"center": v(267.1, 10.1) * mm, "radius": 2 * mm});
            skCircle(sketch, "E9.0.32.8", {"center": v(267.1, 26.1) * mm, "radius": 2 * mm});
            skCircle(sketch, "E9.0.32.9", {"center": v(267.1, 42.1) * mm, "radius": 2 * mm});
            skCircle(sketch, "E9.0.32.10", {"center": v(267.1, 58.1) * mm, "radius": 2 * mm});
            skCircle(sketch, "E9.0.32.11", {"center": v(267.1, 74.1) * mm, "radius": 2 * mm});
            skCircle(sketch, "E9.0.32.12", {"center": v(267.1, 90.1) * mm, "radius": 2 * mm});
            skCircle(sketch, "E10.0.31.0", {"center": v(243.1, -109.9) * mm, "radius": 2 * mm});
            skCircle(sketch, "E10.0.31.1", {"center": v(243.1, -93.9) * mm, "radius": 2 * mm});
            skCircle(sketch, "E10.0.31.2", {"center": v(243.1, -77.9) * mm, "radius": 2 * mm});
            skCircle(sketch, "E10.0.31.3", {"center": v(243.1, -61.9) * mm, "radius": 2 * mm});
            skCircle(sketch, "E10.0.31.4", {"center": v(243.1, -45.9) * mm, "radius": 2 * mm});
            skCircle(sketch, "E10.0.31.5", {"center": v(243.1, -29.9) * mm, "radius": 2 * mm});
            skCircle(sketch, "E10.0.31.6", {"center": v(243.1, -13.9) * mm, "radius": 2 * mm});
            skCircle(sketch, "E10.0.31.7", {"center": v(243.1, 2.1) * mm, "radius": 2 * mm});
            skCircle(sketch, "E10.0.31.8", {"center": v(243.1, 18.1) * mm, "radius": 2 * mm});
            skCircle(sketch, "E10.0.31.9", {"center": v(243.1, 34.1) * mm, "radius": 2 * mm});
            skCircle(sketch, "E10.0.31.10", {"center": v(243.1, 50.1) * mm, "radius": 2 * mm});
            skCircle(sketch, "E10.0.31.11", {"center": v(243.1, 66.1) * mm, "radius": 2 * mm});
            skCircle(sketch, "E10.0.31.12", {"center": v(243.1, 82.1) * mm, "radius": 2 * mm});
            skCircle(sketch, "E10.0.32.0", {"center": v(259.1, -109.9) * mm, "radius": 2 * mm});
            skCircle(sketch, "E10.0.32.1", {"center": v(259.1, -93.9) * mm, "radius": 2 * mm});
            skCircle(sketch, "E10.0.32.2", {"center": v(259.1, -77.9) * mm, "radius": 2 * mm});
            skCircle(sketch, "E10.0.32.3", {"center": v(259.1, -61.9) * mm, "radius": 2 * mm});
            skCircle(sketch, "E10.0.32.4", {"center": v(259.1, -45.9) * mm, "radius": 2 * mm});
            skCircle(sketch, "E10.0.32.5", {"center": v(259.1, -29.9) * mm, "radius": 2 * mm});
            skCircle(sketch, "E10.0.32.6", {"center": v(259.1, -13.9) * mm, "radius": 2 * mm});
            skCircle(sketch, "E10.0.32.7", {"center": v(259.1, 2.1) * mm, "radius": 2 * mm});
            skCircle(sketch, "E10.0.32.8", {"center": v(259.1, 18.1) * mm, "radius": 2 * mm});
            skCircle(sketch, "E10.0.32.9", {"center": v(259.1, 34.1) * mm, "radius": 2 * mm});
            skCircle(sketch, "E10.0.32.10", {"center": v(259.1, 50.1) * mm, "radius": 2 * mm});
            skCircle(sketch, "E10.0.32.11", {"center": v(259.1, 66.1) * mm, "radius": 2 * mm});
            skCircle(sketch, "E10.0.32.12", {"center": v(259.1, 82.1) * mm, "radius": 2 * mm});
            skCircle(sketch, "E11.0.0.13", {"center": v(-244.9, 106.1) * mm, "radius": 2 * mm});
            skCircle(sketch, "E11.0.1.13", {"center": v(-228.9, 106.1) * mm, "radius": 2 * mm});
            skCircle(sketch, "E11.0.2.13", {"center": v(-212.9, 106.1) * mm, "radius": 2 * mm});
            skCircle(sketch, "E11.0.3.13", {"center": v(-196.9, 106.1) * mm, "radius": 2 * mm});
            skCircle(sketch, "E11.0.4.13", {"center": v(-180.9, 106.1) * mm, "radius": 2 * mm});
            skCircle(sketch, "E11.0.5.13", {"center": v(-164.9, 106.1) * mm, "radius": 2 * mm});
            skCircle(sketch, "E11.0.6.13", {"center": v(-148.9, 106.1) * mm, "radius": 2 * mm});
            skCircle(sketch, "E11.0.7.13", {"center": v(-132.9, 106.1) * mm, "radius": 2 * mm});
            skCircle(sketch, "E11.0.8.13", {"center": v(-116.9, 106.1) * mm, "radius": 2 * mm});
            skCircle(sketch, "E11.0.9.13", {"center": v(-100.9, 106.1) * mm, "radius": 2 * mm});
            skCircle(sketch, "E11.0.10.13", {"center": v(-84.9, 106.1) * mm, "radius": 2 * mm});
            skCircle(sketch, "E11.0.11.13", {"center": v(-68.9, 106.1) * mm, "radius": 2 * mm});
            skCircle(sketch, "E11.0.12.13", {"center": v(-52.9, 106.1) * mm, "radius": 2 * mm});
            skCircle(sketch, "E11.0.13.13", {"center": v(-36.9, 106.1) * mm, "radius": 2 * mm});
            skCircle(sketch, "E11.0.14.13", {"center": v(-20.9, 106.1) * mm, "radius": 2 * mm});
            skCircle(sketch, "E11.0.15.13", {"center": v(-4.9, 106.1) * mm, "radius": 2 * mm});
            skCircle(sketch, "E11.0.16.13", {"center": v(11.1, 106.1) * mm, "radius": 2 * mm});
            skCircle(sketch, "E11.0.17.13", {"center": v(27.1, 106.1) * mm, "radius": 2 * mm});
            skCircle(sketch, "E11.0.18.13", {"center": v(43.1, 106.1) * mm, "radius": 2 * mm});
            skCircle(sketch, "E11.0.19.13", {"center": v(59.1, 106.1) * mm, "radius": 2 * mm});
            skCircle(sketch, "E11.0.20.13", {"center": v(75.1, 106.1) * mm, "radius": 2 * mm});
            skCircle(sketch, "E11.0.21.13", {"center": v(91.1, 106.1) * mm, "radius": 2 * mm});
            skCircle(sketch, "E11.0.22.13", {"center": v(107.1, 106.1) * mm, "radius": 2 * mm});
            skCircle(sketch, "E11.0.23.13", {"center": v(123.1, 106.1) * mm, "radius": 2 * mm});
            skCircle(sketch, "E11.0.24.13", {"center": v(139.1, 106.1) * mm, "radius": 2 * mm});
            skCircle(sketch, "E11.0.25.13", {"center": v(155.1, 106.1) * mm, "radius": 2 * mm});
            skCircle(sketch, "E11.0.26.13", {"center": v(171.1, 106.1) * mm, "radius": 2 * mm});
            skCircle(sketch, "E11.0.27.13", {"center": v(187.1, 106.1) * mm, "radius": 2 * mm});
            skCircle(sketch, "E11.0.28.13", {"center": v(203.1, 106.1) * mm, "radius": 2 * mm});
            skCircle(sketch, "E11.0.29.13", {"center": v(219.1, 106.1) * mm, "radius": 2 * mm});
            skCircle(sketch, "E11.0.30.13", {"center": v(235.1, 106.1) * mm, "radius": 2 * mm});
            skCircle(sketch, "E11.0.31.13", {"center": v(251.1, 106.1) * mm, "radius": 2 * mm});
            skCircle(sketch, "E11.0.32.13", {"center": v(267.1, 106.1) * mm, "radius": 2 * mm});
            skCircle(sketch, "E12.0.0.13", {"center": v(-252.9, 98.1) * mm, "radius": 2 * mm});
            skCircle(sketch, "E12.0.1.13", {"center": v(-236.9, 98.1) * mm, "radius": 2 * mm});
            skCircle(sketch, "E12.0.2.13", {"center": v(-220.9, 98.1) * mm, "radius": 2 * mm});
            skCircle(sketch, "E12.0.3.13", {"center": v(-204.9, 98.1) * mm, "radius": 2 * mm});
            skCircle(sketch, "E12.0.4.13", {"center": v(-188.9, 98.1) * mm, "radius": 2 * mm});
            skCircle(sketch, "E12.0.5.13", {"center": v(-172.9, 98.1) * mm, "radius": 2 * mm});
            skCircle(sketch, "E12.0.6.13", {"center": v(-156.9, 98.1) * mm, "radius": 2 * mm});
            skCircle(sketch, "E12.0.7.13", {"center": v(-140.9, 98.1) * mm, "radius": 2 * mm});
            skCircle(sketch, "E12.0.8.13", {"center": v(-124.9, 98.1) * mm, "radius": 2 * mm});
            skCircle(sketch, "E12.0.9.13", {"center": v(-108.9, 98.1) * mm, "radius": 2 * mm});
            skCircle(sketch, "E12.0.10.13", {"center": v(-92.9, 98.1) * mm, "radius": 2 * mm});
            skCircle(sketch, "E12.0.11.13", {"center": v(-76.9, 98.1) * mm, "radius": 2 * mm});
            skCircle(sketch, "E12.0.12.13", {"center": v(-60.9, 98.1) * mm, "radius": 2 * mm});
            skCircle(sketch, "E12.0.13.13", {"center": v(-44.9, 98.1) * mm, "radius": 2 * mm});
            skCircle(sketch, "E12.0.14.13", {"center": v(-28.9, 98.1) * mm, "radius": 2 * mm});
            skCircle(sketch, "E12.0.15.13", {"center": v(-12.9, 98.1) * mm, "radius": 2 * mm});
            skCircle(sketch, "E12.0.16.13", {"center": v(3.1, 98.1) * mm, "radius": 2 * mm});
            skCircle(sketch, "E12.0.17.13", {"center": v(19.1, 98.1) * mm, "radius": 2 * mm});
            skCircle(sketch, "E12.0.18.13", {"center": v(35.1, 98.1) * mm, "radius": 2 * mm});
            skCircle(sketch, "E12.0.19.13", {"center": v(51.1, 98.1) * mm, "radius": 2 * mm});
            skCircle(sketch, "E12.0.20.13", {"center": v(67.1, 98.1) * mm, "radius": 2 * mm});
            skCircle(sketch, "E12.0.21.13", {"center": v(83.1, 98.1) * mm, "radius": 2 * mm});
            skCircle(sketch, "E12.0.22.13", {"center": v(99.1, 98.1) * mm, "radius": 2 * mm});
            skCircle(sketch, "E12.0.23.13", {"center": v(115.1, 98.1) * mm, "radius": 2 * mm});
            skCircle(sketch, "E12.0.24.13", {"center": v(131.1, 98.1) * mm, "radius": 2 * mm});
            skCircle(sketch, "E12.0.25.13", {"center": v(147.1, 98.1) * mm, "radius": 2 * mm});
            skCircle(sketch, "E12.0.26.13", {"center": v(163.1, 98.1) * mm, "radius": 2 * mm});
            skCircle(sketch, "E12.0.27.13", {"center": v(179.1, 98.1) * mm, "radius": 2 * mm});
            skCircle(sketch, "E12.0.28.13", {"center": v(195.1, 98.1) * mm, "radius": 2 * mm});
            skCircle(sketch, "E12.0.29.13", {"center": v(211.1, 98.1) * mm, "radius": 2 * mm});
            skCircle(sketch, "E12.0.30.13", {"center": v(227.1, 98.1) * mm, "radius": 2 * mm});
            skCircle(sketch, "E12.0.31.13", {"center": v(243.1, 98.1) * mm, "radius": 2 * mm});
            skCircle(sketch, "E12.0.32.13", {"center": v(259.1, 98.1) * mm, "radius": 2 * mm});
            skSolve(sketch);
        }
        {
            var Q0;
            {var subQ131=sQuery(id+"F0.wireOp",EDGE,"E0.right");Q0=makeQuery(id+"F0.imprint","IMPRINT",FACE,{"disambiguationData":[TD([[makeQuery(id+"F0.imprint","IMPRINT",EDGE,{"derivedFrom":subQ131}),-1.0]])]});}
            extrude(context, id + "F1", {"entities" : qUnion([Q0]), "depth" : 1 * mm, "offsetDistance" : 25 * mm});
        }
    });
